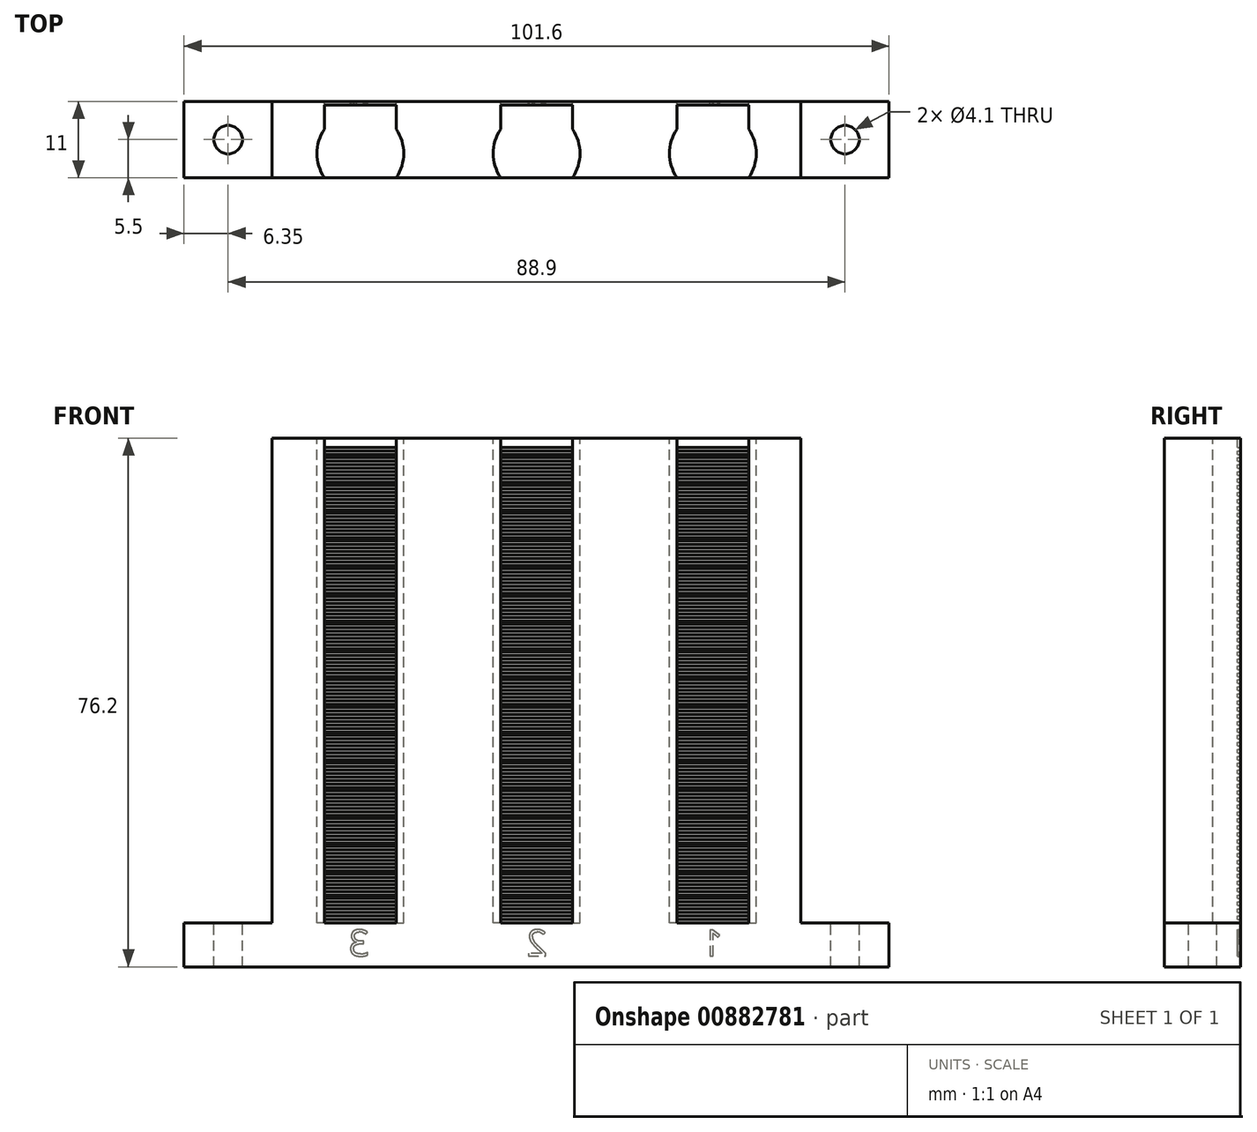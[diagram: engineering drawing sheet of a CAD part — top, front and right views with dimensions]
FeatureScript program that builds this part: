
annotation { "Feature Type Name" : "Feature", "Feature Type Description" : "" }
export const myFeature = defineFeature(function(context is Context, id is Id, definition is map)
    precondition{}
    {
        {
            var Q0;
            Q0=qCreatedBy(makeId("Top.planeOp"),FACE);
            var sketch = newSketch(context, id + "F0", { "sketchPlane" : qUnion([Q0])});
            skLineSegment(sketch, "E0.bottom", {"start": v(38.1, -5.5) * mm, "end": v(-38.1, -5.5) * mm});
            skLineSegment(sketch, "E0.top", {"start": v(38.1, 5.5) * mm, "end": v(-38.1, 5.5) * mm});
            skLineSegment(sketch, "E0.left", {"start": v(38.1, -5.5) * mm, "end": v(38.1, 5.5) * mm});
            skLineSegment(sketch, "E0.right", {"start": v(-38.1, -5.5) * mm, "end": v(-38.1, 5.5) * mm});
            skPoint(sketch, "E0.middle", {"position": v(0, 0) * mm});
            skSolve(sketch);
        }
        {
            var Q0;
            Q0 = qSketchRegion(id + "F0", true);
            extrude(context, id + "F1", {"entities" : qUnion([Q0]), "depth" : 76.2 * mm, "offsetDistance" : 25.4 * mm});
        }
        {
            var Q0;
            Q0=makeQuery(id+"F1.opExtrude","CAP_FACE",FACE,{"disambiguationData":[OSD([sQuery(id+"F0.wireOp",EDGE,"E0.bottom"),sQuery(id+"F0.wireOp",EDGE,"E0.top"),sQuery(id+"F0.wireOp",EDGE,"E0.left"),sQuery(id+"F0.wireOp",EDGE,"E0.right")])],"isStart":false});
            var sketch = newSketch(context, id + "F2", { "sketchPlane" : qUnion([Q0])});
            skLineSegment(sketch, "E1", {"start": v(0, 5.5) * mm, "end": v(0, -5.5) * mm});
            skCircle(sketch, "E2", {"center": v(0, -2) * mm, "radius": 6.25 * mm});
            skCircle(sketch, "E3", {"center": v(-25.4, -2) * mm, "radius": 6.25 * mm});
            skCircle(sketch, "E4", {"center": v(25.4, -2) * mm, "radius": 6.25 * mm});
            skSolve(sketch);
        }
        {
            var Q0;
            Q0 = qSketchRegion(id + "F2", true);
            extrude(context, id + "F3", {"entities" : qUnion([Q0]), "operationType" : NewBodyOperationType.REMOVE, "oppositeDirection" : true, "depth" : 69.85 * mm, "offsetDistance" : 25.4 * mm});
        }
        {
            var Q0;
            Q0=makeQuery(id+"F1.opExtrude","SWEPT_FACE",FACE,{"disambiguationData":[OSD([sQuery(id+"F0.wireOp",EDGE,"E0.top")])]});
            var sketch = newSketch(context, id + "F4", { "sketchPlane" : qUnion([Q0])});
            skLineSegment(sketch, "E5.bottom", {"start": v(-30.58, 6.35) * mm, "end": v(-20.22, 6.35) * mm});
            skLineSegment(sketch, "E5.top", {"start": v(-30.58, 6.85) * mm, "end": v(-20.22, 6.85) * mm});
            skLineSegment(sketch, "E5.left", {"start": v(-30.58, 6.35) * mm, "end": v(-30.58, 6.85) * mm});
            skLineSegment(sketch, "E5.right", {"start": v(-20.22, 6.35) * mm, "end": v(-20.22, 6.85) * mm});
            skLineSegment(sketch, "E6.0.1.0", {"start": v(-30.58, 7.35) * mm, "end": v(-20.22, 7.35) * mm});
            skLineSegment(sketch, "E6.0.1.1", {"start": v(-30.58, 7.85) * mm, "end": v(-20.22, 7.85) * mm});
            skLineSegment(sketch, "E6.0.1.2", {"start": v(-30.58, 7.35) * mm, "end": v(-30.58, 7.85) * mm});
            skLineSegment(sketch, "E6.0.1.3", {"start": v(-20.22, 7.35) * mm, "end": v(-20.22, 7.85) * mm});
            skLineSegment(sketch, "E6.0.2.0", {"start": v(-30.58, 8.35) * mm, "end": v(-20.22, 8.35) * mm});
            skLineSegment(sketch, "E6.0.2.1", {"start": v(-30.58, 8.85) * mm, "end": v(-20.22, 8.85) * mm});
            skLineSegment(sketch, "E6.0.2.2", {"start": v(-30.58, 8.35) * mm, "end": v(-30.58, 8.85) * mm});
            skLineSegment(sketch, "E6.0.2.3", {"start": v(-20.22, 8.35) * mm, "end": v(-20.22, 8.85) * mm});
            skLineSegment(sketch, "E6.0.3.0", {"start": v(-30.58, 9.35) * mm, "end": v(-20.22, 9.35) * mm});
            skLineSegment(sketch, "E6.0.3.1", {"start": v(-30.58, 9.85) * mm, "end": v(-20.22, 9.85) * mm});
            skLineSegment(sketch, "E6.0.3.2", {"start": v(-30.58, 9.35) * mm, "end": v(-30.58, 9.85) * mm});
            skLineSegment(sketch, "E6.0.3.3", {"start": v(-20.22, 9.35) * mm, "end": v(-20.22, 9.85) * mm});
            skLineSegment(sketch, "E6.0.4.0", {"start": v(-30.58, 10.35) * mm, "end": v(-20.22, 10.35) * mm});
            skLineSegment(sketch, "E6.0.4.1", {"start": v(-30.58, 10.85) * mm, "end": v(-20.22, 10.85) * mm});
            skLineSegment(sketch, "E6.0.4.2", {"start": v(-30.58, 10.35) * mm, "end": v(-30.58, 10.85) * mm});
            skLineSegment(sketch, "E6.0.4.3", {"start": v(-20.22, 10.35) * mm, "end": v(-20.22, 10.85) * mm});
            skLineSegment(sketch, "E6.0.5.0", {"start": v(-30.58, 11.35) * mm, "end": v(-20.22, 11.35) * mm});
            skLineSegment(sketch, "E6.0.5.1", {"start": v(-30.58, 11.85) * mm, "end": v(-20.22, 11.85) * mm});
            skLineSegment(sketch, "E6.0.5.2", {"start": v(-30.58, 11.35) * mm, "end": v(-30.58, 11.85) * mm});
            skLineSegment(sketch, "E6.0.5.3", {"start": v(-20.22, 11.35) * mm, "end": v(-20.22, 11.85) * mm});
            skLineSegment(sketch, "E6.0.6.0", {"start": v(-30.58, 12.35) * mm, "end": v(-20.22, 12.35) * mm});
            skLineSegment(sketch, "E6.0.6.1", {"start": v(-30.58, 12.85) * mm, "end": v(-20.22, 12.85) * mm});
            skLineSegment(sketch, "E6.0.6.2", {"start": v(-30.58, 12.35) * mm, "end": v(-30.58, 12.85) * mm});
            skLineSegment(sketch, "E6.0.6.3", {"start": v(-20.22, 12.35) * mm, "end": v(-20.22, 12.85) * mm});
            skLineSegment(sketch, "E6.0.7.0", {"start": v(-30.58, 13.35) * mm, "end": v(-20.22, 13.35) * mm});
            skLineSegment(sketch, "E6.0.7.1", {"start": v(-30.58, 13.85) * mm, "end": v(-20.22, 13.85) * mm});
            skLineSegment(sketch, "E6.0.7.2", {"start": v(-30.58, 13.35) * mm, "end": v(-30.58, 13.85) * mm});
            skLineSegment(sketch, "E6.0.7.3", {"start": v(-20.22, 13.35) * mm, "end": v(-20.22, 13.85) * mm});
            skLineSegment(sketch, "E6.0.8.0", {"start": v(-30.58, 14.35) * mm, "end": v(-20.22, 14.35) * mm});
            skLineSegment(sketch, "E6.0.8.1", {"start": v(-30.58, 14.85) * mm, "end": v(-20.22, 14.85) * mm});
            skLineSegment(sketch, "E6.0.8.2", {"start": v(-30.58, 14.35) * mm, "end": v(-30.58, 14.85) * mm});
            skLineSegment(sketch, "E6.0.8.3", {"start": v(-20.22, 14.35) * mm, "end": v(-20.22, 14.85) * mm});
            skLineSegment(sketch, "E6.0.9.0", {"start": v(-30.58, 15.35) * mm, "end": v(-20.22, 15.35) * mm});
            skLineSegment(sketch, "E6.0.9.1", {"start": v(-30.58, 15.85) * mm, "end": v(-20.22, 15.85) * mm});
            skLineSegment(sketch, "E6.0.9.2", {"start": v(-30.58, 15.35) * mm, "end": v(-30.58, 15.85) * mm});
            skLineSegment(sketch, "E6.0.9.3", {"start": v(-20.22, 15.35) * mm, "end": v(-20.22, 15.85) * mm});
            skLineSegment(sketch, "E6.0.10.0", {"start": v(-30.58, 16.35) * mm, "end": v(-20.22, 16.35) * mm});
            skLineSegment(sketch, "E6.0.10.1", {"start": v(-30.58, 16.85) * mm, "end": v(-20.22, 16.85) * mm});
            skLineSegment(sketch, "E6.0.10.2", {"start": v(-30.58, 16.35) * mm, "end": v(-30.58, 16.85) * mm});
            skLineSegment(sketch, "E6.0.10.3", {"start": v(-20.22, 16.35) * mm, "end": v(-20.22, 16.85) * mm});
            skLineSegment(sketch, "E6.0.11.0", {"start": v(-30.58, 17.35) * mm, "end": v(-20.22, 17.35) * mm});
            skLineSegment(sketch, "E6.0.11.1", {"start": v(-30.58, 17.85) * mm, "end": v(-20.22, 17.85) * mm});
            skLineSegment(sketch, "E6.0.11.2", {"start": v(-30.58, 17.35) * mm, "end": v(-30.58, 17.85) * mm});
            skLineSegment(sketch, "E6.0.11.3", {"start": v(-20.22, 17.35) * mm, "end": v(-20.22, 17.85) * mm});
            skLineSegment(sketch, "E6.0.12.0", {"start": v(-30.58, 18.35) * mm, "end": v(-20.22, 18.35) * mm});
            skLineSegment(sketch, "E6.0.12.1", {"start": v(-30.58, 18.85) * mm, "end": v(-20.22, 18.85) * mm});
            skLineSegment(sketch, "E6.0.12.2", {"start": v(-30.58, 18.35) * mm, "end": v(-30.58, 18.85) * mm});
            skLineSegment(sketch, "E6.0.12.3", {"start": v(-20.22, 18.35) * mm, "end": v(-20.22, 18.85) * mm});
            skLineSegment(sketch, "E6.0.13.0", {"start": v(-30.58, 19.35) * mm, "end": v(-20.22, 19.35) * mm});
            skLineSegment(sketch, "E6.0.13.1", {"start": v(-30.58, 19.85) * mm, "end": v(-20.22, 19.85) * mm});
            skLineSegment(sketch, "E6.0.13.2", {"start": v(-30.58, 19.35) * mm, "end": v(-30.58, 19.85) * mm});
            skLineSegment(sketch, "E6.0.13.3", {"start": v(-20.22, 19.35) * mm, "end": v(-20.22, 19.85) * mm});
            skLineSegment(sketch, "E6.0.14.0", {"start": v(-30.58, 20.35) * mm, "end": v(-20.22, 20.35) * mm});
            skLineSegment(sketch, "E6.0.14.1", {"start": v(-30.58, 20.85) * mm, "end": v(-20.22, 20.85) * mm});
            skLineSegment(sketch, "E6.0.14.2", {"start": v(-30.58, 20.35) * mm, "end": v(-30.58, 20.85) * mm});
            skLineSegment(sketch, "E6.0.14.3", {"start": v(-20.22, 20.35) * mm, "end": v(-20.22, 20.85) * mm});
            skLineSegment(sketch, "E6.0.15.0", {"start": v(-30.58, 21.35) * mm, "end": v(-20.22, 21.35) * mm});
            skLineSegment(sketch, "E6.0.15.1", {"start": v(-30.58, 21.85) * mm, "end": v(-20.22, 21.85) * mm});
            skLineSegment(sketch, "E6.0.15.2", {"start": v(-30.58, 21.35) * mm, "end": v(-30.58, 21.85) * mm});
            skLineSegment(sketch, "E6.0.15.3", {"start": v(-20.22, 21.35) * mm, "end": v(-20.22, 21.85) * mm});
            skLineSegment(sketch, "E6.1.0.0", {"start": v(-5.18, 6.35) * mm, "end": v(5.18, 6.35) * mm});
            skLineSegment(sketch, "E6.1.0.1", {"start": v(-5.18, 6.85) * mm, "end": v(5.18, 6.85) * mm});
            skLineSegment(sketch, "E6.1.0.2", {"start": v(-5.18, 6.35) * mm, "end": v(-5.18, 6.85) * mm});
            skLineSegment(sketch, "E6.1.0.3", {"start": v(5.18, 6.35) * mm, "end": v(5.18, 6.85) * mm});
            skLineSegment(sketch, "E6.1.1.0", {"start": v(-5.18, 7.35) * mm, "end": v(5.18, 7.35) * mm});
            skLineSegment(sketch, "E6.1.1.1", {"start": v(-5.18, 7.85) * mm, "end": v(5.18, 7.85) * mm});
            skLineSegment(sketch, "E6.1.1.2", {"start": v(-5.18, 7.35) * mm, "end": v(-5.18, 7.85) * mm});
            skLineSegment(sketch, "E6.1.1.3", {"start": v(5.18, 7.35) * mm, "end": v(5.18, 7.85) * mm});
            skLineSegment(sketch, "E6.1.2.0", {"start": v(-5.18, 8.35) * mm, "end": v(5.18, 8.35) * mm});
            skLineSegment(sketch, "E6.1.2.1", {"start": v(-5.18, 8.85) * mm, "end": v(5.18, 8.85) * mm});
            skLineSegment(sketch, "E6.1.2.2", {"start": v(-5.18, 8.35) * mm, "end": v(-5.18, 8.85) * mm});
            skLineSegment(sketch, "E6.1.2.3", {"start": v(5.18, 8.35) * mm, "end": v(5.18, 8.85) * mm});
            skLineSegment(sketch, "E6.1.3.0", {"start": v(-5.18, 9.35) * mm, "end": v(5.18, 9.35) * mm});
            skLineSegment(sketch, "E6.1.3.1", {"start": v(-5.18, 9.85) * mm, "end": v(5.18, 9.85) * mm});
            skLineSegment(sketch, "E6.1.3.2", {"start": v(-5.18, 9.35) * mm, "end": v(-5.18, 9.85) * mm});
            skLineSegment(sketch, "E6.1.3.3", {"start": v(5.18, 9.35) * mm, "end": v(5.18, 9.85) * mm});
            skLineSegment(sketch, "E6.1.4.0", {"start": v(-5.18, 10.35) * mm, "end": v(5.18, 10.35) * mm});
            skLineSegment(sketch, "E6.1.4.1", {"start": v(-5.18, 10.85) * mm, "end": v(5.18, 10.85) * mm});
            skLineSegment(sketch, "E6.1.4.2", {"start": v(-5.18, 10.35) * mm, "end": v(-5.18, 10.85) * mm});
            skLineSegment(sketch, "E6.1.4.3", {"start": v(5.18, 10.35) * mm, "end": v(5.18, 10.85) * mm});
            skLineSegment(sketch, "E6.1.5.0", {"start": v(-5.18, 11.35) * mm, "end": v(5.18, 11.35) * mm});
            skLineSegment(sketch, "E6.1.5.1", {"start": v(-5.18, 11.85) * mm, "end": v(5.18, 11.85) * mm});
            skLineSegment(sketch, "E6.1.5.2", {"start": v(-5.18, 11.35) * mm, "end": v(-5.18, 11.85) * mm});
            skLineSegment(sketch, "E6.1.5.3", {"start": v(5.18, 11.35) * mm, "end": v(5.18, 11.85) * mm});
            skLineSegment(sketch, "E6.1.6.0", {"start": v(-5.18, 12.35) * mm, "end": v(5.18, 12.35) * mm});
            skLineSegment(sketch, "E6.1.6.1", {"start": v(-5.18, 12.85) * mm, "end": v(5.18, 12.85) * mm});
            skLineSegment(sketch, "E6.1.6.2", {"start": v(-5.18, 12.35) * mm, "end": v(-5.18, 12.85) * mm});
            skLineSegment(sketch, "E6.1.6.3", {"start": v(5.18, 12.35) * mm, "end": v(5.18, 12.85) * mm});
            skLineSegment(sketch, "E6.1.7.0", {"start": v(-5.18, 13.35) * mm, "end": v(5.18, 13.35) * mm});
            skLineSegment(sketch, "E6.1.7.1", {"start": v(-5.18, 13.85) * mm, "end": v(5.18, 13.85) * mm});
            skLineSegment(sketch, "E6.1.7.2", {"start": v(-5.18, 13.35) * mm, "end": v(-5.18, 13.85) * mm});
            skLineSegment(sketch, "E6.1.7.3", {"start": v(5.18, 13.35) * mm, "end": v(5.18, 13.85) * mm});
            skLineSegment(sketch, "E6.1.8.0", {"start": v(-5.18, 14.35) * mm, "end": v(5.18, 14.35) * mm});
            skLineSegment(sketch, "E6.1.8.1", {"start": v(-5.18, 14.85) * mm, "end": v(5.18, 14.85) * mm});
            skLineSegment(sketch, "E6.1.8.2", {"start": v(-5.18, 14.35) * mm, "end": v(-5.18, 14.85) * mm});
            skLineSegment(sketch, "E6.1.8.3", {"start": v(5.18, 14.35) * mm, "end": v(5.18, 14.85) * mm});
            skLineSegment(sketch, "E6.1.9.0", {"start": v(-5.18, 15.35) * mm, "end": v(5.18, 15.35) * mm});
            skLineSegment(sketch, "E6.1.9.1", {"start": v(-5.18, 15.85) * mm, "end": v(5.18, 15.85) * mm});
            skLineSegment(sketch, "E6.1.9.2", {"start": v(-5.18, 15.35) * mm, "end": v(-5.18, 15.85) * mm});
            skLineSegment(sketch, "E6.1.9.3", {"start": v(5.18, 15.35) * mm, "end": v(5.18, 15.85) * mm});
            skLineSegment(sketch, "E6.1.10.0", {"start": v(-5.18, 16.35) * mm, "end": v(5.18, 16.35) * mm});
            skLineSegment(sketch, "E6.1.10.1", {"start": v(-5.18, 16.85) * mm, "end": v(5.18, 16.85) * mm});
            skLineSegment(sketch, "E6.1.10.2", {"start": v(-5.18, 16.35) * mm, "end": v(-5.18, 16.85) * mm});
            skLineSegment(sketch, "E6.1.10.3", {"start": v(5.18, 16.35) * mm, "end": v(5.18, 16.85) * mm});
            skLineSegment(sketch, "E6.1.11.0", {"start": v(-5.18, 17.35) * mm, "end": v(5.18, 17.35) * mm});
            skLineSegment(sketch, "E6.1.11.1", {"start": v(-5.18, 17.85) * mm, "end": v(5.18, 17.85) * mm});
            skLineSegment(sketch, "E6.1.11.2", {"start": v(-5.18, 17.35) * mm, "end": v(-5.18, 17.85) * mm});
            skLineSegment(sketch, "E6.1.11.3", {"start": v(5.18, 17.35) * mm, "end": v(5.18, 17.85) * mm});
            skLineSegment(sketch, "E6.1.12.0", {"start": v(-5.18, 18.35) * mm, "end": v(5.18, 18.35) * mm});
            skLineSegment(sketch, "E6.1.12.1", {"start": v(-5.18, 18.85) * mm, "end": v(5.18, 18.85) * mm});
            skLineSegment(sketch, "E6.1.12.2", {"start": v(-5.18, 18.35) * mm, "end": v(-5.18, 18.85) * mm});
            skLineSegment(sketch, "E6.1.12.3", {"start": v(5.18, 18.35) * mm, "end": v(5.18, 18.85) * mm});
            skLineSegment(sketch, "E6.1.13.0", {"start": v(-5.18, 19.35) * mm, "end": v(5.18, 19.35) * mm});
            skLineSegment(sketch, "E6.1.13.1", {"start": v(-5.18, 19.85) * mm, "end": v(5.18, 19.85) * mm});
            skLineSegment(sketch, "E6.1.13.2", {"start": v(-5.18, 19.35) * mm, "end": v(-5.18, 19.85) * mm});
            skLineSegment(sketch, "E6.1.13.3", {"start": v(5.18, 19.35) * mm, "end": v(5.18, 19.85) * mm});
            skLineSegment(sketch, "E6.1.14.0", {"start": v(-5.18, 20.35) * mm, "end": v(5.18, 20.35) * mm});
            skLineSegment(sketch, "E6.1.14.1", {"start": v(-5.18, 20.85) * mm, "end": v(5.18, 20.85) * mm});
            skLineSegment(sketch, "E6.1.14.2", {"start": v(-5.18, 20.35) * mm, "end": v(-5.18, 20.85) * mm});
            skLineSegment(sketch, "E6.1.14.3", {"start": v(5.18, 20.35) * mm, "end": v(5.18, 20.85) * mm});
            skLineSegment(sketch, "E6.1.15.0", {"start": v(-5.18, 21.35) * mm, "end": v(5.18, 21.35) * mm});
            skLineSegment(sketch, "E6.1.15.1", {"start": v(-5.18, 21.85) * mm, "end": v(5.18, 21.85) * mm});
            skLineSegment(sketch, "E6.1.15.2", {"start": v(-5.18, 21.35) * mm, "end": v(-5.18, 21.85) * mm});
            skLineSegment(sketch, "E6.1.15.3", {"start": v(5.18, 21.35) * mm, "end": v(5.18, 21.85) * mm});
            skLineSegment(sketch, "E6.2.0.0", {"start": v(20.22, 6.35) * mm, "end": v(30.58, 6.35) * mm});
            skLineSegment(sketch, "E6.2.0.1", {"start": v(20.22, 6.85) * mm, "end": v(30.58, 6.85) * mm});
            skLineSegment(sketch, "E6.2.0.2", {"start": v(20.22, 6.35) * mm, "end": v(20.22, 6.85) * mm});
            skLineSegment(sketch, "E6.2.0.3", {"start": v(30.58, 6.35) * mm, "end": v(30.58, 6.85) * mm});
            skLineSegment(sketch, "E6.2.1.0", {"start": v(20.22, 7.35) * mm, "end": v(30.58, 7.35) * mm});
            skLineSegment(sketch, "E6.2.1.1", {"start": v(20.22, 7.85) * mm, "end": v(30.58, 7.85) * mm});
            skLineSegment(sketch, "E6.2.1.2", {"start": v(20.22, 7.35) * mm, "end": v(20.22, 7.85) * mm});
            skLineSegment(sketch, "E6.2.1.3", {"start": v(30.58, 7.35) * mm, "end": v(30.58, 7.85) * mm});
            skLineSegment(sketch, "E6.2.2.0", {"start": v(20.22, 8.35) * mm, "end": v(30.58, 8.35) * mm});
            skLineSegment(sketch, "E6.2.2.1", {"start": v(20.22, 8.85) * mm, "end": v(30.58, 8.85) * mm});
            skLineSegment(sketch, "E6.2.2.2", {"start": v(20.22, 8.35) * mm, "end": v(20.22, 8.85) * mm});
            skLineSegment(sketch, "E6.2.2.3", {"start": v(30.58, 8.35) * mm, "end": v(30.58, 8.85) * mm});
            skLineSegment(sketch, "E6.2.3.0", {"start": v(20.22, 9.35) * mm, "end": v(30.58, 9.35) * mm});
            skLineSegment(sketch, "E6.2.3.1", {"start": v(20.22, 9.85) * mm, "end": v(30.58, 9.85) * mm});
            skLineSegment(sketch, "E6.2.3.2", {"start": v(20.22, 9.35) * mm, "end": v(20.22, 9.85) * mm});
            skLineSegment(sketch, "E6.2.3.3", {"start": v(30.58, 9.35) * mm, "end": v(30.58, 9.85) * mm});
            skLineSegment(sketch, "E6.2.4.0", {"start": v(20.22, 10.35) * mm, "end": v(30.58, 10.35) * mm});
            skLineSegment(sketch, "E6.2.4.1", {"start": v(20.22, 10.85) * mm, "end": v(30.58, 10.85) * mm});
            skLineSegment(sketch, "E6.2.4.2", {"start": v(20.22, 10.35) * mm, "end": v(20.22, 10.85) * mm});
            skLineSegment(sketch, "E6.2.4.3", {"start": v(30.58, 10.35) * mm, "end": v(30.58, 10.85) * mm});
            skLineSegment(sketch, "E6.2.5.0", {"start": v(20.22, 11.35) * mm, "end": v(30.58, 11.35) * mm});
            skLineSegment(sketch, "E6.2.5.1", {"start": v(20.22, 11.85) * mm, "end": v(30.58, 11.85) * mm});
            skLineSegment(sketch, "E6.2.5.2", {"start": v(20.22, 11.35) * mm, "end": v(20.22, 11.85) * mm});
            skLineSegment(sketch, "E6.2.5.3", {"start": v(30.58, 11.35) * mm, "end": v(30.58, 11.85) * mm});
            skLineSegment(sketch, "E6.2.6.0", {"start": v(20.22, 12.35) * mm, "end": v(30.58, 12.35) * mm});
            skLineSegment(sketch, "E6.2.6.1", {"start": v(20.22, 12.85) * mm, "end": v(30.58, 12.85) * mm});
            skLineSegment(sketch, "E6.2.6.2", {"start": v(20.22, 12.35) * mm, "end": v(20.22, 12.85) * mm});
            skLineSegment(sketch, "E6.2.6.3", {"start": v(30.58, 12.35) * mm, "end": v(30.58, 12.85) * mm});
            skLineSegment(sketch, "E6.2.7.0", {"start": v(20.22, 13.35) * mm, "end": v(30.58, 13.35) * mm});
            skLineSegment(sketch, "E6.2.7.1", {"start": v(20.22, 13.85) * mm, "end": v(30.58, 13.85) * mm});
            skLineSegment(sketch, "E6.2.7.2", {"start": v(20.22, 13.35) * mm, "end": v(20.22, 13.85) * mm});
            skLineSegment(sketch, "E6.2.7.3", {"start": v(30.58, 13.35) * mm, "end": v(30.58, 13.85) * mm});
            skLineSegment(sketch, "E6.2.8.0", {"start": v(20.22, 14.35) * mm, "end": v(30.58, 14.35) * mm});
            skLineSegment(sketch, "E6.2.8.1", {"start": v(20.22, 14.85) * mm, "end": v(30.58, 14.85) * mm});
            skLineSegment(sketch, "E6.2.8.2", {"start": v(20.22, 14.35) * mm, "end": v(20.22, 14.85) * mm});
            skLineSegment(sketch, "E6.2.8.3", {"start": v(30.58, 14.35) * mm, "end": v(30.58, 14.85) * mm});
            skLineSegment(sketch, "E6.2.9.0", {"start": v(20.22, 15.35) * mm, "end": v(30.58, 15.35) * mm});
            skLineSegment(sketch, "E6.2.9.1", {"start": v(20.22, 15.85) * mm, "end": v(30.58, 15.85) * mm});
            skLineSegment(sketch, "E6.2.9.2", {"start": v(20.22, 15.35) * mm, "end": v(20.22, 15.85) * mm});
            skLineSegment(sketch, "E6.2.9.3", {"start": v(30.58, 15.35) * mm, "end": v(30.58, 15.85) * mm});
            skLineSegment(sketch, "E6.2.10.0", {"start": v(20.22, 16.35) * mm, "end": v(30.58, 16.35) * mm});
            skLineSegment(sketch, "E6.2.10.1", {"start": v(20.22, 16.85) * mm, "end": v(30.58, 16.85) * mm});
            skLineSegment(sketch, "E6.2.10.2", {"start": v(20.22, 16.35) * mm, "end": v(20.22, 16.85) * mm});
            skLineSegment(sketch, "E6.2.10.3", {"start": v(30.58, 16.35) * mm, "end": v(30.58, 16.85) * mm});
            skLineSegment(sketch, "E6.2.11.0", {"start": v(20.22, 17.35) * mm, "end": v(30.58, 17.35) * mm});
            skLineSegment(sketch, "E6.2.11.1", {"start": v(20.22, 17.85) * mm, "end": v(30.58, 17.85) * mm});
            skLineSegment(sketch, "E6.2.11.2", {"start": v(20.22, 17.35) * mm, "end": v(20.22, 17.85) * mm});
            skLineSegment(sketch, "E6.2.11.3", {"start": v(30.58, 17.35) * mm, "end": v(30.58, 17.85) * mm});
            skLineSegment(sketch, "E6.2.12.0", {"start": v(20.22, 18.35) * mm, "end": v(30.58, 18.35) * mm});
            skLineSegment(sketch, "E6.2.12.1", {"start": v(20.22, 18.85) * mm, "end": v(30.58, 18.85) * mm});
            skLineSegment(sketch, "E6.2.12.2", {"start": v(20.22, 18.35) * mm, "end": v(20.22, 18.85) * mm});
            skLineSegment(sketch, "E6.2.12.3", {"start": v(30.58, 18.35) * mm, "end": v(30.58, 18.85) * mm});
            skLineSegment(sketch, "E6.2.13.0", {"start": v(20.22, 19.35) * mm, "end": v(30.58, 19.35) * mm});
            skLineSegment(sketch, "E6.2.13.1", {"start": v(20.22, 19.85) * mm, "end": v(30.58, 19.85) * mm});
            skLineSegment(sketch, "E6.2.13.2", {"start": v(20.22, 19.35) * mm, "end": v(20.22, 19.85) * mm});
            skLineSegment(sketch, "E6.2.13.3", {"start": v(30.58, 19.35) * mm, "end": v(30.58, 19.85) * mm});
            skLineSegment(sketch, "E6.2.14.0", {"start": v(20.22, 20.35) * mm, "end": v(30.58, 20.35) * mm});
            skLineSegment(sketch, "E6.2.14.1", {"start": v(20.22, 20.85) * mm, "end": v(30.58, 20.85) * mm});
            skLineSegment(sketch, "E6.2.14.2", {"start": v(20.22, 20.35) * mm, "end": v(20.22, 20.85) * mm});
            skLineSegment(sketch, "E6.2.14.3", {"start": v(30.58, 20.35) * mm, "end": v(30.58, 20.85) * mm});
            skLineSegment(sketch, "E6.2.15.0", {"start": v(20.22, 21.35) * mm, "end": v(30.58, 21.35) * mm});
            skLineSegment(sketch, "E6.2.15.1", {"start": v(20.22, 21.85) * mm, "end": v(30.58, 21.85) * mm});
            skLineSegment(sketch, "E6.2.15.2", {"start": v(20.22, 21.35) * mm, "end": v(20.22, 21.85) * mm});
            skLineSegment(sketch, "E6.2.15.3", {"start": v(30.58, 21.35) * mm, "end": v(30.58, 21.85) * mm});
            skLineSegment(sketch, "E6.direction1", {"start": v(-30.58, 6.35) * mm, "end": v(-5.18, 6.35) * mm, "construction": true});
            skLineSegment(sketch, "E6.direction2", {"start": v(-30.58, 6.35) * mm, "end": v(-30.58, 7.35) * mm, "construction": true});
            skLineSegment(sketch, "E7.0.0.16", {"start": v(-30.58, 22.35) * mm, "end": v(-20.22, 22.35) * mm});
            skLineSegment(sketch, "E7.3.0.16", {"start": v(-30.58, 22.85) * mm, "end": v(-20.22, 22.85) * mm});
            skLineSegment(sketch, "E7.6.0.16", {"start": v(-30.58, 22.35) * mm, "end": v(-30.58, 22.85) * mm});
            skLineSegment(sketch, "E7.9.0.16", {"start": v(-20.22, 22.35) * mm, "end": v(-20.22, 22.85) * mm});
            skLineSegment(sketch, "E7.0.0.17", {"start": v(-30.58, 23.35) * mm, "end": v(-20.22, 23.35) * mm});
            skLineSegment(sketch, "E7.3.0.17", {"start": v(-30.58, 23.85) * mm, "end": v(-20.22, 23.85) * mm});
            skLineSegment(sketch, "E7.6.0.17", {"start": v(-30.58, 23.35) * mm, "end": v(-30.58, 23.85) * mm});
            skLineSegment(sketch, "E7.9.0.17", {"start": v(-20.22, 23.35) * mm, "end": v(-20.22, 23.85) * mm});
            skLineSegment(sketch, "E7.0.1.16", {"start": v(-5.18, 22.35) * mm, "end": v(5.18, 22.35) * mm});
            skLineSegment(sketch, "E7.3.1.16", {"start": v(-5.18, 22.85) * mm, "end": v(5.18, 22.85) * mm});
            skLineSegment(sketch, "E7.6.1.16", {"start": v(-5.18, 22.35) * mm, "end": v(-5.18, 22.85) * mm});
            skLineSegment(sketch, "E7.9.1.16", {"start": v(5.18, 22.35) * mm, "end": v(5.18, 22.85) * mm});
            skLineSegment(sketch, "E7.0.1.17", {"start": v(-5.18, 23.35) * mm, "end": v(5.18, 23.35) * mm});
            skLineSegment(sketch, "E7.3.1.17", {"start": v(-5.18, 23.85) * mm, "end": v(5.18, 23.85) * mm});
            skLineSegment(sketch, "E7.6.1.17", {"start": v(-5.18, 23.35) * mm, "end": v(-5.18, 23.85) * mm});
            skLineSegment(sketch, "E7.9.1.17", {"start": v(5.18, 23.35) * mm, "end": v(5.18, 23.85) * mm});
            skLineSegment(sketch, "E7.0.2.16", {"start": v(20.22, 22.35) * mm, "end": v(30.58, 22.35) * mm});
            skLineSegment(sketch, "E7.3.2.16", {"start": v(20.22, 22.85) * mm, "end": v(30.58, 22.85) * mm});
            skLineSegment(sketch, "E7.6.2.16", {"start": v(20.22, 22.35) * mm, "end": v(20.22, 22.85) * mm});
            skLineSegment(sketch, "E7.9.2.16", {"start": v(30.58, 22.35) * mm, "end": v(30.58, 22.85) * mm});
            skLineSegment(sketch, "E7.0.2.17", {"start": v(20.22, 23.35) * mm, "end": v(30.58, 23.35) * mm});
            skLineSegment(sketch, "E7.3.2.17", {"start": v(20.22, 23.85) * mm, "end": v(30.58, 23.85) * mm});
            skLineSegment(sketch, "E7.6.2.17", {"start": v(20.22, 23.35) * mm, "end": v(20.22, 23.85) * mm});
            skLineSegment(sketch, "E7.9.2.17", {"start": v(30.58, 23.35) * mm, "end": v(30.58, 23.85) * mm});
            skLineSegment(sketch, "E8.0.0.18", {"start": v(-30.58, 24.35) * mm, "end": v(-20.22, 24.35) * mm});
            skLineSegment(sketch, "E8.3.0.18", {"start": v(-30.58, 24.85) * mm, "end": v(-20.22, 24.85) * mm});
            skLineSegment(sketch, "E8.6.0.18", {"start": v(-30.58, 24.35) * mm, "end": v(-30.58, 24.85) * mm});
            skLineSegment(sketch, "E8.9.0.18", {"start": v(-20.22, 24.35) * mm, "end": v(-20.22, 24.85) * mm});
            skLineSegment(sketch, "E8.0.0.19", {"start": v(-30.58, 25.35) * mm, "end": v(-20.22, 25.35) * mm});
            skLineSegment(sketch, "E8.3.0.19", {"start": v(-30.58, 25.85) * mm, "end": v(-20.22, 25.85) * mm});
            skLineSegment(sketch, "E8.6.0.19", {"start": v(-30.58, 25.35) * mm, "end": v(-30.58, 25.85) * mm});
            skLineSegment(sketch, "E8.9.0.19", {"start": v(-20.22, 25.35) * mm, "end": v(-20.22, 25.85) * mm});
            skLineSegment(sketch, "E8.0.0.20", {"start": v(-30.58, 26.35) * mm, "end": v(-20.22, 26.35) * mm});
            skLineSegment(sketch, "E8.3.0.20", {"start": v(-30.58, 26.85) * mm, "end": v(-20.22, 26.85) * mm});
            skLineSegment(sketch, "E8.6.0.20", {"start": v(-30.58, 26.35) * mm, "end": v(-30.58, 26.85) * mm});
            skLineSegment(sketch, "E8.9.0.20", {"start": v(-20.22, 26.35) * mm, "end": v(-20.22, 26.85) * mm});
            skLineSegment(sketch, "E8.0.0.21", {"start": v(-30.58, 27.35) * mm, "end": v(-20.22, 27.35) * mm});
            skLineSegment(sketch, "E8.3.0.21", {"start": v(-30.58, 27.85) * mm, "end": v(-20.22, 27.85) * mm});
            skLineSegment(sketch, "E8.6.0.21", {"start": v(-30.58, 27.35) * mm, "end": v(-30.58, 27.85) * mm});
            skLineSegment(sketch, "E8.9.0.21", {"start": v(-20.22, 27.35) * mm, "end": v(-20.22, 27.85) * mm});
            skLineSegment(sketch, "E8.0.0.22", {"start": v(-30.58, 28.35) * mm, "end": v(-20.22, 28.35) * mm});
            skLineSegment(sketch, "E8.3.0.22", {"start": v(-30.58, 28.85) * mm, "end": v(-20.22, 28.85) * mm});
            skLineSegment(sketch, "E8.6.0.22", {"start": v(-30.58, 28.35) * mm, "end": v(-30.58, 28.85) * mm});
            skLineSegment(sketch, "E8.9.0.22", {"start": v(-20.22, 28.35) * mm, "end": v(-20.22, 28.85) * mm});
            skLineSegment(sketch, "E8.0.0.23", {"start": v(-30.58, 29.35) * mm, "end": v(-20.22, 29.35) * mm});
            skLineSegment(sketch, "E8.3.0.23", {"start": v(-30.58, 29.85) * mm, "end": v(-20.22, 29.85) * mm});
            skLineSegment(sketch, "E8.6.0.23", {"start": v(-30.58, 29.35) * mm, "end": v(-30.58, 29.85) * mm});
            skLineSegment(sketch, "E8.9.0.23", {"start": v(-20.22, 29.35) * mm, "end": v(-20.22, 29.85) * mm});
            skLineSegment(sketch, "E8.0.0.24", {"start": v(-30.58, 30.35) * mm, "end": v(-20.22, 30.35) * mm});
            skLineSegment(sketch, "E8.3.0.24", {"start": v(-30.58, 30.85) * mm, "end": v(-20.22, 30.85) * mm});
            skLineSegment(sketch, "E8.6.0.24", {"start": v(-30.58, 30.35) * mm, "end": v(-30.58, 30.85) * mm});
            skLineSegment(sketch, "E8.9.0.24", {"start": v(-20.22, 30.35) * mm, "end": v(-20.22, 30.85) * mm});
            skLineSegment(sketch, "E8.0.0.25", {"start": v(-30.58, 31.35) * mm, "end": v(-20.22, 31.35) * mm});
            skLineSegment(sketch, "E8.3.0.25", {"start": v(-30.58, 31.85) * mm, "end": v(-20.22, 31.85) * mm});
            skLineSegment(sketch, "E8.6.0.25", {"start": v(-30.58, 31.35) * mm, "end": v(-30.58, 31.85) * mm});
            skLineSegment(sketch, "E8.9.0.25", {"start": v(-20.22, 31.35) * mm, "end": v(-20.22, 31.85) * mm});
            skLineSegment(sketch, "E8.0.0.26", {"start": v(-30.58, 32.35) * mm, "end": v(-20.22, 32.35) * mm});
            skLineSegment(sketch, "E8.3.0.26", {"start": v(-30.58, 32.85) * mm, "end": v(-20.22, 32.85) * mm});
            skLineSegment(sketch, "E8.6.0.26", {"start": v(-30.58, 32.35) * mm, "end": v(-30.58, 32.85) * mm});
            skLineSegment(sketch, "E8.9.0.26", {"start": v(-20.22, 32.35) * mm, "end": v(-20.22, 32.85) * mm});
            skLineSegment(sketch, "E8.0.0.27", {"start": v(-30.58, 33.35) * mm, "end": v(-20.22, 33.35) * mm});
            skLineSegment(sketch, "E8.3.0.27", {"start": v(-30.58, 33.85) * mm, "end": v(-20.22, 33.85) * mm});
            skLineSegment(sketch, "E8.6.0.27", {"start": v(-30.58, 33.35) * mm, "end": v(-30.58, 33.85) * mm});
            skLineSegment(sketch, "E8.9.0.27", {"start": v(-20.22, 33.35) * mm, "end": v(-20.22, 33.85) * mm});
            skLineSegment(sketch, "E8.0.0.28", {"start": v(-30.58, 34.35) * mm, "end": v(-20.22, 34.35) * mm});
            skLineSegment(sketch, "E8.3.0.28", {"start": v(-30.58, 34.85) * mm, "end": v(-20.22, 34.85) * mm});
            skLineSegment(sketch, "E8.6.0.28", {"start": v(-30.58, 34.35) * mm, "end": v(-30.58, 34.85) * mm});
            skLineSegment(sketch, "E8.9.0.28", {"start": v(-20.22, 34.35) * mm, "end": v(-20.22, 34.85) * mm});
            skLineSegment(sketch, "E8.0.0.29", {"start": v(-30.58, 35.35) * mm, "end": v(-20.22, 35.35) * mm});
            skLineSegment(sketch, "E8.3.0.29", {"start": v(-30.58, 35.85) * mm, "end": v(-20.22, 35.85) * mm});
            skLineSegment(sketch, "E8.6.0.29", {"start": v(-30.58, 35.35) * mm, "end": v(-30.58, 35.85) * mm});
            skLineSegment(sketch, "E8.9.0.29", {"start": v(-20.22, 35.35) * mm, "end": v(-20.22, 35.85) * mm});
            skLineSegment(sketch, "E8.0.0.30", {"start": v(-30.58, 36.35) * mm, "end": v(-20.22, 36.35) * mm});
            skLineSegment(sketch, "E8.3.0.30", {"start": v(-30.58, 36.85) * mm, "end": v(-20.22, 36.85) * mm});
            skLineSegment(sketch, "E8.6.0.30", {"start": v(-30.58, 36.35) * mm, "end": v(-30.58, 36.85) * mm});
            skLineSegment(sketch, "E8.9.0.30", {"start": v(-20.22, 36.35) * mm, "end": v(-20.22, 36.85) * mm});
            skLineSegment(sketch, "E8.0.0.31", {"start": v(-30.58, 37.35) * mm, "end": v(-20.22, 37.35) * mm});
            skLineSegment(sketch, "E8.3.0.31", {"start": v(-30.58, 37.85) * mm, "end": v(-20.22, 37.85) * mm});
            skLineSegment(sketch, "E8.6.0.31", {"start": v(-30.58, 37.35) * mm, "end": v(-30.58, 37.85) * mm});
            skLineSegment(sketch, "E8.9.0.31", {"start": v(-20.22, 37.35) * mm, "end": v(-20.22, 37.85) * mm});
            skLineSegment(sketch, "E8.0.0.32", {"start": v(-30.58, 38.35) * mm, "end": v(-20.22, 38.35) * mm});
            skLineSegment(sketch, "E8.3.0.32", {"start": v(-30.58, 38.85) * mm, "end": v(-20.22, 38.85) * mm});
            skLineSegment(sketch, "E8.6.0.32", {"start": v(-30.58, 38.35) * mm, "end": v(-30.58, 38.85) * mm});
            skLineSegment(sketch, "E8.9.0.32", {"start": v(-20.22, 38.35) * mm, "end": v(-20.22, 38.85) * mm});
            skLineSegment(sketch, "E8.0.0.33", {"start": v(-30.58, 39.35) * mm, "end": v(-20.22, 39.35) * mm});
            skLineSegment(sketch, "E8.3.0.33", {"start": v(-30.58, 39.85) * mm, "end": v(-20.22, 39.85) * mm});
            skLineSegment(sketch, "E8.6.0.33", {"start": v(-30.58, 39.35) * mm, "end": v(-30.58, 39.85) * mm});
            skLineSegment(sketch, "E8.9.0.33", {"start": v(-20.22, 39.35) * mm, "end": v(-20.22, 39.85) * mm});
            skLineSegment(sketch, "E8.0.0.34", {"start": v(-30.58, 40.35) * mm, "end": v(-20.22, 40.35) * mm});
            skLineSegment(sketch, "E8.3.0.34", {"start": v(-30.58, 40.85) * mm, "end": v(-20.22, 40.85) * mm});
            skLineSegment(sketch, "E8.6.0.34", {"start": v(-30.58, 40.35) * mm, "end": v(-30.58, 40.85) * mm});
            skLineSegment(sketch, "E8.9.0.34", {"start": v(-20.22, 40.35) * mm, "end": v(-20.22, 40.85) * mm});
            skLineSegment(sketch, "E8.0.0.35", {"start": v(-30.58, 41.35) * mm, "end": v(-20.22, 41.35) * mm});
            skLineSegment(sketch, "E8.3.0.35", {"start": v(-30.58, 41.85) * mm, "end": v(-20.22, 41.85) * mm});
            skLineSegment(sketch, "E8.6.0.35", {"start": v(-30.58, 41.35) * mm, "end": v(-30.58, 41.85) * mm});
            skLineSegment(sketch, "E8.9.0.35", {"start": v(-20.22, 41.35) * mm, "end": v(-20.22, 41.85) * mm});
            skLineSegment(sketch, "E8.0.0.36", {"start": v(-30.58, 42.35) * mm, "end": v(-20.22, 42.35) * mm});
            skLineSegment(sketch, "E8.3.0.36", {"start": v(-30.58, 42.85) * mm, "end": v(-20.22, 42.85) * mm});
            skLineSegment(sketch, "E8.6.0.36", {"start": v(-30.58, 42.35) * mm, "end": v(-30.58, 42.85) * mm});
            skLineSegment(sketch, "E8.9.0.36", {"start": v(-20.22, 42.35) * mm, "end": v(-20.22, 42.85) * mm});
            skLineSegment(sketch, "E8.0.0.37", {"start": v(-30.58, 43.35) * mm, "end": v(-20.22, 43.35) * mm});
            skLineSegment(sketch, "E8.3.0.37", {"start": v(-30.58, 43.85) * mm, "end": v(-20.22, 43.85) * mm});
            skLineSegment(sketch, "E8.6.0.37", {"start": v(-30.58, 43.35) * mm, "end": v(-30.58, 43.85) * mm});
            skLineSegment(sketch, "E8.9.0.37", {"start": v(-20.22, 43.35) * mm, "end": v(-20.22, 43.85) * mm});
            skLineSegment(sketch, "E8.0.0.38", {"start": v(-30.58, 44.35) * mm, "end": v(-20.22, 44.35) * mm});
            skLineSegment(sketch, "E8.3.0.38", {"start": v(-30.58, 44.85) * mm, "end": v(-20.22, 44.85) * mm});
            skLineSegment(sketch, "E8.6.0.38", {"start": v(-30.58, 44.35) * mm, "end": v(-30.58, 44.85) * mm});
            skLineSegment(sketch, "E8.9.0.38", {"start": v(-20.22, 44.35) * mm, "end": v(-20.22, 44.85) * mm});
            skLineSegment(sketch, "E8.0.0.39", {"start": v(-30.58, 45.35) * mm, "end": v(-20.22, 45.35) * mm});
            skLineSegment(sketch, "E8.3.0.39", {"start": v(-30.58, 45.85) * mm, "end": v(-20.22, 45.85) * mm});
            skLineSegment(sketch, "E8.6.0.39", {"start": v(-30.58, 45.35) * mm, "end": v(-30.58, 45.85) * mm});
            skLineSegment(sketch, "E8.9.0.39", {"start": v(-20.22, 45.35) * mm, "end": v(-20.22, 45.85) * mm});
            skLineSegment(sketch, "E8.0.0.40", {"start": v(-30.58, 46.35) * mm, "end": v(-20.22, 46.35) * mm});
            skLineSegment(sketch, "E8.3.0.40", {"start": v(-30.58, 46.85) * mm, "end": v(-20.22, 46.85) * mm});
            skLineSegment(sketch, "E8.6.0.40", {"start": v(-30.58, 46.35) * mm, "end": v(-30.58, 46.85) * mm});
            skLineSegment(sketch, "E8.9.0.40", {"start": v(-20.22, 46.35) * mm, "end": v(-20.22, 46.85) * mm});
            skLineSegment(sketch, "E8.0.0.41", {"start": v(-30.58, 47.35) * mm, "end": v(-20.22, 47.35) * mm});
            skLineSegment(sketch, "E8.3.0.41", {"start": v(-30.58, 47.85) * mm, "end": v(-20.22, 47.85) * mm});
            skLineSegment(sketch, "E8.6.0.41", {"start": v(-30.58, 47.35) * mm, "end": v(-30.58, 47.85) * mm});
            skLineSegment(sketch, "E8.9.0.41", {"start": v(-20.22, 47.35) * mm, "end": v(-20.22, 47.85) * mm});
            skLineSegment(sketch, "E8.0.0.42", {"start": v(-30.58, 48.35) * mm, "end": v(-20.22, 48.35) * mm});
            skLineSegment(sketch, "E8.3.0.42", {"start": v(-30.58, 48.85) * mm, "end": v(-20.22, 48.85) * mm});
            skLineSegment(sketch, "E8.6.0.42", {"start": v(-30.58, 48.35) * mm, "end": v(-30.58, 48.85) * mm});
            skLineSegment(sketch, "E8.9.0.42", {"start": v(-20.22, 48.35) * mm, "end": v(-20.22, 48.85) * mm});
            skLineSegment(sketch, "E8.0.0.43", {"start": v(-30.58, 49.35) * mm, "end": v(-20.22, 49.35) * mm});
            skLineSegment(sketch, "E8.3.0.43", {"start": v(-30.58, 49.85) * mm, "end": v(-20.22, 49.85) * mm});
            skLineSegment(sketch, "E8.6.0.43", {"start": v(-30.58, 49.35) * mm, "end": v(-30.58, 49.85) * mm});
            skLineSegment(sketch, "E8.9.0.43", {"start": v(-20.22, 49.35) * mm, "end": v(-20.22, 49.85) * mm});
            skLineSegment(sketch, "E8.0.0.44", {"start": v(-30.58, 50.35) * mm, "end": v(-20.22, 50.35) * mm});
            skLineSegment(sketch, "E8.3.0.44", {"start": v(-30.58, 50.85) * mm, "end": v(-20.22, 50.85) * mm});
            skLineSegment(sketch, "E8.6.0.44", {"start": v(-30.58, 50.35) * mm, "end": v(-30.58, 50.85) * mm});
            skLineSegment(sketch, "E8.9.0.44", {"start": v(-20.22, 50.35) * mm, "end": v(-20.22, 50.85) * mm});
            skLineSegment(sketch, "E8.0.0.45", {"start": v(-30.58, 51.35) * mm, "end": v(-20.22, 51.35) * mm});
            skLineSegment(sketch, "E8.3.0.45", {"start": v(-30.58, 51.85) * mm, "end": v(-20.22, 51.85) * mm});
            skLineSegment(sketch, "E8.6.0.45", {"start": v(-30.58, 51.35) * mm, "end": v(-30.58, 51.85) * mm});
            skLineSegment(sketch, "E8.9.0.45", {"start": v(-20.22, 51.35) * mm, "end": v(-20.22, 51.85) * mm});
            skLineSegment(sketch, "E8.0.0.46", {"start": v(-30.58, 52.35) * mm, "end": v(-20.22, 52.35) * mm});
            skLineSegment(sketch, "E8.3.0.46", {"start": v(-30.58, 52.85) * mm, "end": v(-20.22, 52.85) * mm});
            skLineSegment(sketch, "E8.6.0.46", {"start": v(-30.58, 52.35) * mm, "end": v(-30.58, 52.85) * mm});
            skLineSegment(sketch, "E8.9.0.46", {"start": v(-20.22, 52.35) * mm, "end": v(-20.22, 52.85) * mm});
            skLineSegment(sketch, "E8.0.0.47", {"start": v(-30.58, 53.35) * mm, "end": v(-20.22, 53.35) * mm});
            skLineSegment(sketch, "E8.3.0.47", {"start": v(-30.58, 53.85) * mm, "end": v(-20.22, 53.85) * mm});
            skLineSegment(sketch, "E8.6.0.47", {"start": v(-30.58, 53.35) * mm, "end": v(-30.58, 53.85) * mm});
            skLineSegment(sketch, "E8.9.0.47", {"start": v(-20.22, 53.35) * mm, "end": v(-20.22, 53.85) * mm});
            skLineSegment(sketch, "E8.0.0.48", {"start": v(-30.58, 54.35) * mm, "end": v(-20.22, 54.35) * mm});
            skLineSegment(sketch, "E8.3.0.48", {"start": v(-30.58, 54.85) * mm, "end": v(-20.22, 54.85) * mm});
            skLineSegment(sketch, "E8.6.0.48", {"start": v(-30.58, 54.35) * mm, "end": v(-30.58, 54.85) * mm});
            skLineSegment(sketch, "E8.9.0.48", {"start": v(-20.22, 54.35) * mm, "end": v(-20.22, 54.85) * mm});
            skLineSegment(sketch, "E8.0.0.49", {"start": v(-30.58, 55.35) * mm, "end": v(-20.22, 55.35) * mm});
            skLineSegment(sketch, "E8.3.0.49", {"start": v(-30.58, 55.85) * mm, "end": v(-20.22, 55.85) * mm});
            skLineSegment(sketch, "E8.6.0.49", {"start": v(-30.58, 55.35) * mm, "end": v(-30.58, 55.85) * mm});
            skLineSegment(sketch, "E8.9.0.49", {"start": v(-20.22, 55.35) * mm, "end": v(-20.22, 55.85) * mm});
            skLineSegment(sketch, "E8.0.0.50", {"start": v(-30.58, 56.35) * mm, "end": v(-20.22, 56.35) * mm});
            skLineSegment(sketch, "E8.3.0.50", {"start": v(-30.58, 56.85) * mm, "end": v(-20.22, 56.85) * mm});
            skLineSegment(sketch, "E8.6.0.50", {"start": v(-30.58, 56.35) * mm, "end": v(-30.58, 56.85) * mm});
            skLineSegment(sketch, "E8.9.0.50", {"start": v(-20.22, 56.35) * mm, "end": v(-20.22, 56.85) * mm});
            skLineSegment(sketch, "E8.0.0.51", {"start": v(-30.58, 57.35) * mm, "end": v(-20.22, 57.35) * mm});
            skLineSegment(sketch, "E8.3.0.51", {"start": v(-30.58, 57.85) * mm, "end": v(-20.22, 57.85) * mm});
            skLineSegment(sketch, "E8.6.0.51", {"start": v(-30.58, 57.35) * mm, "end": v(-30.58, 57.85) * mm});
            skLineSegment(sketch, "E8.9.0.51", {"start": v(-20.22, 57.35) * mm, "end": v(-20.22, 57.85) * mm});
            skLineSegment(sketch, "E8.0.0.52", {"start": v(-30.58, 58.35) * mm, "end": v(-20.22, 58.35) * mm});
            skLineSegment(sketch, "E8.3.0.52", {"start": v(-30.58, 58.85) * mm, "end": v(-20.22, 58.85) * mm});
            skLineSegment(sketch, "E8.6.0.52", {"start": v(-30.58, 58.35) * mm, "end": v(-30.58, 58.85) * mm});
            skLineSegment(sketch, "E8.9.0.52", {"start": v(-20.22, 58.35) * mm, "end": v(-20.22, 58.85) * mm});
            skLineSegment(sketch, "E8.0.0.53", {"start": v(-30.58, 59.35) * mm, "end": v(-20.22, 59.35) * mm});
            skLineSegment(sketch, "E8.3.0.53", {"start": v(-30.58, 59.85) * mm, "end": v(-20.22, 59.85) * mm});
            skLineSegment(sketch, "E8.6.0.53", {"start": v(-30.58, 59.35) * mm, "end": v(-30.58, 59.85) * mm});
            skLineSegment(sketch, "E8.9.0.53", {"start": v(-20.22, 59.35) * mm, "end": v(-20.22, 59.85) * mm});
            skLineSegment(sketch, "E8.0.0.54", {"start": v(-30.58, 60.35) * mm, "end": v(-20.22, 60.35) * mm});
            skLineSegment(sketch, "E8.3.0.54", {"start": v(-30.58, 60.85) * mm, "end": v(-20.22, 60.85) * mm});
            skLineSegment(sketch, "E8.6.0.54", {"start": v(-30.58, 60.35) * mm, "end": v(-30.58, 60.85) * mm});
            skLineSegment(sketch, "E8.9.0.54", {"start": v(-20.22, 60.35) * mm, "end": v(-20.22, 60.85) * mm});
            skLineSegment(sketch, "E8.0.0.55", {"start": v(-30.58, 61.35) * mm, "end": v(-20.22, 61.35) * mm});
            skLineSegment(sketch, "E8.3.0.55", {"start": v(-30.58, 61.85) * mm, "end": v(-20.22, 61.85) * mm});
            skLineSegment(sketch, "E8.6.0.55", {"start": v(-30.58, 61.35) * mm, "end": v(-30.58, 61.85) * mm});
            skLineSegment(sketch, "E8.9.0.55", {"start": v(-20.22, 61.35) * mm, "end": v(-20.22, 61.85) * mm});
            skLineSegment(sketch, "E8.0.0.56", {"start": v(-30.58, 62.35) * mm, "end": v(-20.22, 62.35) * mm});
            skLineSegment(sketch, "E8.3.0.56", {"start": v(-30.58, 62.85) * mm, "end": v(-20.22, 62.85) * mm});
            skLineSegment(sketch, "E8.6.0.56", {"start": v(-30.58, 62.35) * mm, "end": v(-30.58, 62.85) * mm});
            skLineSegment(sketch, "E8.9.0.56", {"start": v(-20.22, 62.35) * mm, "end": v(-20.22, 62.85) * mm});
            skLineSegment(sketch, "E8.0.0.57", {"start": v(-30.58, 63.35) * mm, "end": v(-20.22, 63.35) * mm});
            skLineSegment(sketch, "E8.3.0.57", {"start": v(-30.58, 63.85) * mm, "end": v(-20.22, 63.85) * mm});
            skLineSegment(sketch, "E8.6.0.57", {"start": v(-30.58, 63.35) * mm, "end": v(-30.58, 63.85) * mm});
            skLineSegment(sketch, "E8.9.0.57", {"start": v(-20.22, 63.35) * mm, "end": v(-20.22, 63.85) * mm});
            skLineSegment(sketch, "E8.0.0.58", {"start": v(-30.58, 64.35) * mm, "end": v(-20.22, 64.35) * mm});
            skLineSegment(sketch, "E8.3.0.58", {"start": v(-30.58, 64.85) * mm, "end": v(-20.22, 64.85) * mm});
            skLineSegment(sketch, "E8.6.0.58", {"start": v(-30.58, 64.35) * mm, "end": v(-30.58, 64.85) * mm});
            skLineSegment(sketch, "E8.9.0.58", {"start": v(-20.22, 64.35) * mm, "end": v(-20.22, 64.85) * mm});
            skLineSegment(sketch, "E8.0.0.59", {"start": v(-30.58, 65.35) * mm, "end": v(-20.22, 65.35) * mm});
            skLineSegment(sketch, "E8.3.0.59", {"start": v(-30.58, 65.85) * mm, "end": v(-20.22, 65.85) * mm});
            skLineSegment(sketch, "E8.6.0.59", {"start": v(-30.58, 65.35) * mm, "end": v(-30.58, 65.85) * mm});
            skLineSegment(sketch, "E8.9.0.59", {"start": v(-20.22, 65.35) * mm, "end": v(-20.22, 65.85) * mm});
            skLineSegment(sketch, "E8.0.0.60", {"start": v(-30.58, 66.35) * mm, "end": v(-20.22, 66.35) * mm});
            skLineSegment(sketch, "E8.3.0.60", {"start": v(-30.58, 66.85) * mm, "end": v(-20.22, 66.85) * mm});
            skLineSegment(sketch, "E8.6.0.60", {"start": v(-30.58, 66.35) * mm, "end": v(-30.58, 66.85) * mm});
            skLineSegment(sketch, "E8.9.0.60", {"start": v(-20.22, 66.35) * mm, "end": v(-20.22, 66.85) * mm});
            skLineSegment(sketch, "E8.0.0.61", {"start": v(-30.58, 67.35) * mm, "end": v(-20.22, 67.35) * mm});
            skLineSegment(sketch, "E8.3.0.61", {"start": v(-30.58, 67.85) * mm, "end": v(-20.22, 67.85) * mm});
            skLineSegment(sketch, "E8.6.0.61", {"start": v(-30.58, 67.35) * mm, "end": v(-30.58, 67.85) * mm});
            skLineSegment(sketch, "E8.9.0.61", {"start": v(-20.22, 67.35) * mm, "end": v(-20.22, 67.85) * mm});
            skLineSegment(sketch, "E8.0.0.62", {"start": v(-30.58, 68.35) * mm, "end": v(-20.22, 68.35) * mm});
            skLineSegment(sketch, "E8.3.0.62", {"start": v(-30.58, 68.85) * mm, "end": v(-20.22, 68.85) * mm});
            skLineSegment(sketch, "E8.6.0.62", {"start": v(-30.58, 68.35) * mm, "end": v(-30.58, 68.85) * mm});
            skLineSegment(sketch, "E8.9.0.62", {"start": v(-20.22, 68.35) * mm, "end": v(-20.22, 68.85) * mm});
            skLineSegment(sketch, "E8.0.0.63", {"start": v(-30.58, 69.35) * mm, "end": v(-20.22, 69.35) * mm});
            skLineSegment(sketch, "E8.3.0.63", {"start": v(-30.58, 69.85) * mm, "end": v(-20.22, 69.85) * mm});
            skLineSegment(sketch, "E8.6.0.63", {"start": v(-30.58, 69.35) * mm, "end": v(-30.58, 69.85) * mm});
            skLineSegment(sketch, "E8.9.0.63", {"start": v(-20.22, 69.35) * mm, "end": v(-20.22, 69.85) * mm});
            skLineSegment(sketch, "E8.0.0.64", {"start": v(-30.58, 70.35) * mm, "end": v(-20.22, 70.35) * mm});
            skLineSegment(sketch, "E8.3.0.64", {"start": v(-30.58, 70.85) * mm, "end": v(-20.22, 70.85) * mm});
            skLineSegment(sketch, "E8.6.0.64", {"start": v(-30.58, 70.35) * mm, "end": v(-30.58, 70.85) * mm});
            skLineSegment(sketch, "E8.9.0.64", {"start": v(-20.22, 70.35) * mm, "end": v(-20.22, 70.85) * mm});
            skLineSegment(sketch, "E8.0.0.65", {"start": v(-30.58, 71.35) * mm, "end": v(-20.22, 71.35) * mm});
            skLineSegment(sketch, "E8.3.0.65", {"start": v(-30.58, 71.85) * mm, "end": v(-20.22, 71.85) * mm});
            skLineSegment(sketch, "E8.6.0.65", {"start": v(-30.58, 71.35) * mm, "end": v(-30.58, 71.85) * mm});
            skLineSegment(sketch, "E8.9.0.65", {"start": v(-20.22, 71.35) * mm, "end": v(-20.22, 71.85) * mm});
            skLineSegment(sketch, "E8.0.0.66", {"start": v(-30.58, 72.35) * mm, "end": v(-20.22, 72.35) * mm});
            skLineSegment(sketch, "E8.3.0.66", {"start": v(-30.58, 72.85) * mm, "end": v(-20.22, 72.85) * mm});
            skLineSegment(sketch, "E8.6.0.66", {"start": v(-30.58, 72.35) * mm, "end": v(-30.58, 72.85) * mm});
            skLineSegment(sketch, "E8.9.0.66", {"start": v(-20.22, 72.35) * mm, "end": v(-20.22, 72.85) * mm});
            skLineSegment(sketch, "E8.0.0.67", {"start": v(-30.58, 73.35) * mm, "end": v(-20.22, 73.35) * mm});
            skLineSegment(sketch, "E8.3.0.67", {"start": v(-30.58, 73.85) * mm, "end": v(-20.22, 73.85) * mm});
            skLineSegment(sketch, "E8.6.0.67", {"start": v(-30.58, 73.35) * mm, "end": v(-30.58, 73.85) * mm});
            skLineSegment(sketch, "E8.9.0.67", {"start": v(-20.22, 73.35) * mm, "end": v(-20.22, 73.85) * mm});
            skLineSegment(sketch, "E8.0.0.68", {"start": v(-30.58, 74.35) * mm, "end": v(-20.22, 74.35) * mm});
            skLineSegment(sketch, "E8.3.0.68", {"start": v(-30.58, 74.85) * mm, "end": v(-20.22, 74.85) * mm});
            skLineSegment(sketch, "E8.6.0.68", {"start": v(-30.58, 74.35) * mm, "end": v(-30.58, 74.85) * mm});
            skLineSegment(sketch, "E8.9.0.68", {"start": v(-20.22, 74.35) * mm, "end": v(-20.22, 74.85) * mm});
            skLineSegment(sketch, "E8.0.1.18", {"start": v(-5.18, 24.35) * mm, "end": v(5.18, 24.35) * mm});
            skLineSegment(sketch, "E8.3.1.18", {"start": v(-5.18, 24.85) * mm, "end": v(5.18, 24.85) * mm});
            skLineSegment(sketch, "E8.6.1.18", {"start": v(-5.18, 24.35) * mm, "end": v(-5.18, 24.85) * mm});
            skLineSegment(sketch, "E8.9.1.18", {"start": v(5.18, 24.35) * mm, "end": v(5.18, 24.85) * mm});
            skLineSegment(sketch, "E8.0.1.19", {"start": v(-5.18, 25.35) * mm, "end": v(5.18, 25.35) * mm});
            skLineSegment(sketch, "E8.3.1.19", {"start": v(-5.18, 25.85) * mm, "end": v(5.18, 25.85) * mm});
            skLineSegment(sketch, "E8.6.1.19", {"start": v(-5.18, 25.35) * mm, "end": v(-5.18, 25.85) * mm});
            skLineSegment(sketch, "E8.9.1.19", {"start": v(5.18, 25.35) * mm, "end": v(5.18, 25.85) * mm});
            skLineSegment(sketch, "E8.0.1.20", {"start": v(-5.18, 26.35) * mm, "end": v(5.18, 26.35) * mm});
            skLineSegment(sketch, "E8.3.1.20", {"start": v(-5.18, 26.85) * mm, "end": v(5.18, 26.85) * mm});
            skLineSegment(sketch, "E8.6.1.20", {"start": v(-5.18, 26.35) * mm, "end": v(-5.18, 26.85) * mm});
            skLineSegment(sketch, "E8.9.1.20", {"start": v(5.18, 26.35) * mm, "end": v(5.18, 26.85) * mm});
            skLineSegment(sketch, "E8.0.1.21", {"start": v(-5.18, 27.35) * mm, "end": v(5.18, 27.35) * mm});
            skLineSegment(sketch, "E8.3.1.21", {"start": v(-5.18, 27.85) * mm, "end": v(5.18, 27.85) * mm});
            skLineSegment(sketch, "E8.6.1.21", {"start": v(-5.18, 27.35) * mm, "end": v(-5.18, 27.85) * mm});
            skLineSegment(sketch, "E8.9.1.21", {"start": v(5.18, 27.35) * mm, "end": v(5.18, 27.85) * mm});
            skLineSegment(sketch, "E8.0.1.22", {"start": v(-5.18, 28.35) * mm, "end": v(5.18, 28.35) * mm});
            skLineSegment(sketch, "E8.3.1.22", {"start": v(-5.18, 28.85) * mm, "end": v(5.18, 28.85) * mm});
            skLineSegment(sketch, "E8.6.1.22", {"start": v(-5.18, 28.35) * mm, "end": v(-5.18, 28.85) * mm});
            skLineSegment(sketch, "E8.9.1.22", {"start": v(5.18, 28.35) * mm, "end": v(5.18, 28.85) * mm});
            skLineSegment(sketch, "E8.0.1.23", {"start": v(-5.18, 29.35) * mm, "end": v(5.18, 29.35) * mm});
            skLineSegment(sketch, "E8.3.1.23", {"start": v(-5.18, 29.85) * mm, "end": v(5.18, 29.85) * mm});
            skLineSegment(sketch, "E8.6.1.23", {"start": v(-5.18, 29.35) * mm, "end": v(-5.18, 29.85) * mm});
            skLineSegment(sketch, "E8.9.1.23", {"start": v(5.18, 29.35) * mm, "end": v(5.18, 29.85) * mm});
            skLineSegment(sketch, "E8.0.1.24", {"start": v(-5.18, 30.35) * mm, "end": v(5.18, 30.35) * mm});
            skLineSegment(sketch, "E8.3.1.24", {"start": v(-5.18, 30.85) * mm, "end": v(5.18, 30.85) * mm});
            skLineSegment(sketch, "E8.6.1.24", {"start": v(-5.18, 30.35) * mm, "end": v(-5.18, 30.85) * mm});
            skLineSegment(sketch, "E8.9.1.24", {"start": v(5.18, 30.35) * mm, "end": v(5.18, 30.85) * mm});
            skLineSegment(sketch, "E8.0.1.25", {"start": v(-5.18, 31.35) * mm, "end": v(5.18, 31.35) * mm});
            skLineSegment(sketch, "E8.3.1.25", {"start": v(-5.18, 31.85) * mm, "end": v(5.18, 31.85) * mm});
            skLineSegment(sketch, "E8.6.1.25", {"start": v(-5.18, 31.35) * mm, "end": v(-5.18, 31.85) * mm});
            skLineSegment(sketch, "E8.9.1.25", {"start": v(5.18, 31.35) * mm, "end": v(5.18, 31.85) * mm});
            skLineSegment(sketch, "E8.0.1.26", {"start": v(-5.18, 32.35) * mm, "end": v(5.18, 32.35) * mm});
            skLineSegment(sketch, "E8.3.1.26", {"start": v(-5.18, 32.85) * mm, "end": v(5.18, 32.85) * mm});
            skLineSegment(sketch, "E8.6.1.26", {"start": v(-5.18, 32.35) * mm, "end": v(-5.18, 32.85) * mm});
            skLineSegment(sketch, "E8.9.1.26", {"start": v(5.18, 32.35) * mm, "end": v(5.18, 32.85) * mm});
            skLineSegment(sketch, "E8.0.1.27", {"start": v(-5.18, 33.35) * mm, "end": v(5.18, 33.35) * mm});
            skLineSegment(sketch, "E8.3.1.27", {"start": v(-5.18, 33.85) * mm, "end": v(5.18, 33.85) * mm});
            skLineSegment(sketch, "E8.6.1.27", {"start": v(-5.18, 33.35) * mm, "end": v(-5.18, 33.85) * mm});
            skLineSegment(sketch, "E8.9.1.27", {"start": v(5.18, 33.35) * mm, "end": v(5.18, 33.85) * mm});
            skLineSegment(sketch, "E8.0.1.28", {"start": v(-5.18, 34.35) * mm, "end": v(5.18, 34.35) * mm});
            skLineSegment(sketch, "E8.3.1.28", {"start": v(-5.18, 34.85) * mm, "end": v(5.18, 34.85) * mm});
            skLineSegment(sketch, "E8.6.1.28", {"start": v(-5.18, 34.35) * mm, "end": v(-5.18, 34.85) * mm});
            skLineSegment(sketch, "E8.9.1.28", {"start": v(5.18, 34.35) * mm, "end": v(5.18, 34.85) * mm});
            skLineSegment(sketch, "E8.0.1.29", {"start": v(-5.18, 35.35) * mm, "end": v(5.18, 35.35) * mm});
            skLineSegment(sketch, "E8.3.1.29", {"start": v(-5.18, 35.85) * mm, "end": v(5.18, 35.85) * mm});
            skLineSegment(sketch, "E8.6.1.29", {"start": v(-5.18, 35.35) * mm, "end": v(-5.18, 35.85) * mm});
            skLineSegment(sketch, "E8.9.1.29", {"start": v(5.18, 35.35) * mm, "end": v(5.18, 35.85) * mm});
            skLineSegment(sketch, "E8.0.1.30", {"start": v(-5.18, 36.35) * mm, "end": v(5.18, 36.35) * mm});
            skLineSegment(sketch, "E8.3.1.30", {"start": v(-5.18, 36.85) * mm, "end": v(5.18, 36.85) * mm});
            skLineSegment(sketch, "E8.6.1.30", {"start": v(-5.18, 36.35) * mm, "end": v(-5.18, 36.85) * mm});
            skLineSegment(sketch, "E8.9.1.30", {"start": v(5.18, 36.35) * mm, "end": v(5.18, 36.85) * mm});
            skLineSegment(sketch, "E8.0.1.31", {"start": v(-5.18, 37.35) * mm, "end": v(5.18, 37.35) * mm});
            skLineSegment(sketch, "E8.3.1.31", {"start": v(-5.18, 37.85) * mm, "end": v(5.18, 37.85) * mm});
            skLineSegment(sketch, "E8.6.1.31", {"start": v(-5.18, 37.35) * mm, "end": v(-5.18, 37.85) * mm});
            skLineSegment(sketch, "E8.9.1.31", {"start": v(5.18, 37.35) * mm, "end": v(5.18, 37.85) * mm});
            skLineSegment(sketch, "E8.0.1.32", {"start": v(-5.18, 38.35) * mm, "end": v(5.18, 38.35) * mm});
            skLineSegment(sketch, "E8.3.1.32", {"start": v(-5.18, 38.85) * mm, "end": v(5.18, 38.85) * mm});
            skLineSegment(sketch, "E8.6.1.32", {"start": v(-5.18, 38.35) * mm, "end": v(-5.18, 38.85) * mm});
            skLineSegment(sketch, "E8.9.1.32", {"start": v(5.18, 38.35) * mm, "end": v(5.18, 38.85) * mm});
            skLineSegment(sketch, "E8.0.1.33", {"start": v(-5.18, 39.35) * mm, "end": v(5.18, 39.35) * mm});
            skLineSegment(sketch, "E8.3.1.33", {"start": v(-5.18, 39.85) * mm, "end": v(5.18, 39.85) * mm});
            skLineSegment(sketch, "E8.6.1.33", {"start": v(-5.18, 39.35) * mm, "end": v(-5.18, 39.85) * mm});
            skLineSegment(sketch, "E8.9.1.33", {"start": v(5.18, 39.35) * mm, "end": v(5.18, 39.85) * mm});
            skLineSegment(sketch, "E8.0.1.34", {"start": v(-5.18, 40.35) * mm, "end": v(5.18, 40.35) * mm});
            skLineSegment(sketch, "E8.3.1.34", {"start": v(-5.18, 40.85) * mm, "end": v(5.18, 40.85) * mm});
            skLineSegment(sketch, "E8.6.1.34", {"start": v(-5.18, 40.35) * mm, "end": v(-5.18, 40.85) * mm});
            skLineSegment(sketch, "E8.9.1.34", {"start": v(5.18, 40.35) * mm, "end": v(5.18, 40.85) * mm});
            skLineSegment(sketch, "E8.0.1.35", {"start": v(-5.18, 41.35) * mm, "end": v(5.18, 41.35) * mm});
            skLineSegment(sketch, "E8.3.1.35", {"start": v(-5.18, 41.85) * mm, "end": v(5.18, 41.85) * mm});
            skLineSegment(sketch, "E8.6.1.35", {"start": v(-5.18, 41.35) * mm, "end": v(-5.18, 41.85) * mm});
            skLineSegment(sketch, "E8.9.1.35", {"start": v(5.18, 41.35) * mm, "end": v(5.18, 41.85) * mm});
            skLineSegment(sketch, "E8.0.1.36", {"start": v(-5.18, 42.35) * mm, "end": v(5.18, 42.35) * mm});
            skLineSegment(sketch, "E8.3.1.36", {"start": v(-5.18, 42.85) * mm, "end": v(5.18, 42.85) * mm});
            skLineSegment(sketch, "E8.6.1.36", {"start": v(-5.18, 42.35) * mm, "end": v(-5.18, 42.85) * mm});
            skLineSegment(sketch, "E8.9.1.36", {"start": v(5.18, 42.35) * mm, "end": v(5.18, 42.85) * mm});
            skLineSegment(sketch, "E8.0.1.37", {"start": v(-5.18, 43.35) * mm, "end": v(5.18, 43.35) * mm});
            skLineSegment(sketch, "E8.3.1.37", {"start": v(-5.18, 43.85) * mm, "end": v(5.18, 43.85) * mm});
            skLineSegment(sketch, "E8.6.1.37", {"start": v(-5.18, 43.35) * mm, "end": v(-5.18, 43.85) * mm});
            skLineSegment(sketch, "E8.9.1.37", {"start": v(5.18, 43.35) * mm, "end": v(5.18, 43.85) * mm});
            skLineSegment(sketch, "E8.0.1.38", {"start": v(-5.18, 44.35) * mm, "end": v(5.18, 44.35) * mm});
            skLineSegment(sketch, "E8.3.1.38", {"start": v(-5.18, 44.85) * mm, "end": v(5.18, 44.85) * mm});
            skLineSegment(sketch, "E8.6.1.38", {"start": v(-5.18, 44.35) * mm, "end": v(-5.18, 44.85) * mm});
            skLineSegment(sketch, "E8.9.1.38", {"start": v(5.18, 44.35) * mm, "end": v(5.18, 44.85) * mm});
            skLineSegment(sketch, "E8.0.1.39", {"start": v(-5.18, 45.35) * mm, "end": v(5.18, 45.35) * mm});
            skLineSegment(sketch, "E8.3.1.39", {"start": v(-5.18, 45.85) * mm, "end": v(5.18, 45.85) * mm});
            skLineSegment(sketch, "E8.6.1.39", {"start": v(-5.18, 45.35) * mm, "end": v(-5.18, 45.85) * mm});
            skLineSegment(sketch, "E8.9.1.39", {"start": v(5.18, 45.35) * mm, "end": v(5.18, 45.85) * mm});
            skLineSegment(sketch, "E8.0.1.40", {"start": v(-5.18, 46.35) * mm, "end": v(5.18, 46.35) * mm});
            skLineSegment(sketch, "E8.3.1.40", {"start": v(-5.18, 46.85) * mm, "end": v(5.18, 46.85) * mm});
            skLineSegment(sketch, "E8.6.1.40", {"start": v(-5.18, 46.35) * mm, "end": v(-5.18, 46.85) * mm});
            skLineSegment(sketch, "E8.9.1.40", {"start": v(5.18, 46.35) * mm, "end": v(5.18, 46.85) * mm});
            skLineSegment(sketch, "E8.0.1.41", {"start": v(-5.18, 47.35) * mm, "end": v(5.18, 47.35) * mm});
            skLineSegment(sketch, "E8.3.1.41", {"start": v(-5.18, 47.85) * mm, "end": v(5.18, 47.85) * mm});
            skLineSegment(sketch, "E8.6.1.41", {"start": v(-5.18, 47.35) * mm, "end": v(-5.18, 47.85) * mm});
            skLineSegment(sketch, "E8.9.1.41", {"start": v(5.18, 47.35) * mm, "end": v(5.18, 47.85) * mm});
            skLineSegment(sketch, "E8.0.1.42", {"start": v(-5.18, 48.35) * mm, "end": v(5.18, 48.35) * mm});
            skLineSegment(sketch, "E8.3.1.42", {"start": v(-5.18, 48.85) * mm, "end": v(5.18, 48.85) * mm});
            skLineSegment(sketch, "E8.6.1.42", {"start": v(-5.18, 48.35) * mm, "end": v(-5.18, 48.85) * mm});
            skLineSegment(sketch, "E8.9.1.42", {"start": v(5.18, 48.35) * mm, "end": v(5.18, 48.85) * mm});
            skLineSegment(sketch, "E8.0.1.43", {"start": v(-5.18, 49.35) * mm, "end": v(5.18, 49.35) * mm});
            skLineSegment(sketch, "E8.3.1.43", {"start": v(-5.18, 49.85) * mm, "end": v(5.18, 49.85) * mm});
            skLineSegment(sketch, "E8.6.1.43", {"start": v(-5.18, 49.35) * mm, "end": v(-5.18, 49.85) * mm});
            skLineSegment(sketch, "E8.9.1.43", {"start": v(5.18, 49.35) * mm, "end": v(5.18, 49.85) * mm});
            skLineSegment(sketch, "E8.0.1.44", {"start": v(-5.18, 50.35) * mm, "end": v(5.18, 50.35) * mm});
            skLineSegment(sketch, "E8.3.1.44", {"start": v(-5.18, 50.85) * mm, "end": v(5.18, 50.85) * mm});
            skLineSegment(sketch, "E8.6.1.44", {"start": v(-5.18, 50.35) * mm, "end": v(-5.18, 50.85) * mm});
            skLineSegment(sketch, "E8.9.1.44", {"start": v(5.18, 50.35) * mm, "end": v(5.18, 50.85) * mm});
            skLineSegment(sketch, "E8.0.1.45", {"start": v(-5.18, 51.35) * mm, "end": v(5.18, 51.35) * mm});
            skLineSegment(sketch, "E8.3.1.45", {"start": v(-5.18, 51.85) * mm, "end": v(5.18, 51.85) * mm});
            skLineSegment(sketch, "E8.6.1.45", {"start": v(-5.18, 51.35) * mm, "end": v(-5.18, 51.85) * mm});
            skLineSegment(sketch, "E8.9.1.45", {"start": v(5.18, 51.35) * mm, "end": v(5.18, 51.85) * mm});
            skLineSegment(sketch, "E8.0.1.46", {"start": v(-5.18, 52.35) * mm, "end": v(5.18, 52.35) * mm});
            skLineSegment(sketch, "E8.3.1.46", {"start": v(-5.18, 52.85) * mm, "end": v(5.18, 52.85) * mm});
            skLineSegment(sketch, "E8.6.1.46", {"start": v(-5.18, 52.35) * mm, "end": v(-5.18, 52.85) * mm});
            skLineSegment(sketch, "E8.9.1.46", {"start": v(5.18, 52.35) * mm, "end": v(5.18, 52.85) * mm});
            skLineSegment(sketch, "E8.0.1.47", {"start": v(-5.18, 53.35) * mm, "end": v(5.18, 53.35) * mm});
            skLineSegment(sketch, "E8.3.1.47", {"start": v(-5.18, 53.85) * mm, "end": v(5.18, 53.85) * mm});
            skLineSegment(sketch, "E8.6.1.47", {"start": v(-5.18, 53.35) * mm, "end": v(-5.18, 53.85) * mm});
            skLineSegment(sketch, "E8.9.1.47", {"start": v(5.18, 53.35) * mm, "end": v(5.18, 53.85) * mm});
            skLineSegment(sketch, "E8.0.1.48", {"start": v(-5.18, 54.35) * mm, "end": v(5.18, 54.35) * mm});
            skLineSegment(sketch, "E8.3.1.48", {"start": v(-5.18, 54.85) * mm, "end": v(5.18, 54.85) * mm});
            skLineSegment(sketch, "E8.6.1.48", {"start": v(-5.18, 54.35) * mm, "end": v(-5.18, 54.85) * mm});
            skLineSegment(sketch, "E8.9.1.48", {"start": v(5.18, 54.35) * mm, "end": v(5.18, 54.85) * mm});
            skLineSegment(sketch, "E8.0.1.49", {"start": v(-5.18, 55.35) * mm, "end": v(5.18, 55.35) * mm});
            skLineSegment(sketch, "E8.3.1.49", {"start": v(-5.18, 55.85) * mm, "end": v(5.18, 55.85) * mm});
            skLineSegment(sketch, "E8.6.1.49", {"start": v(-5.18, 55.35) * mm, "end": v(-5.18, 55.85) * mm});
            skLineSegment(sketch, "E8.9.1.49", {"start": v(5.18, 55.35) * mm, "end": v(5.18, 55.85) * mm});
            skLineSegment(sketch, "E8.0.1.50", {"start": v(-5.18, 56.35) * mm, "end": v(5.18, 56.35) * mm});
            skLineSegment(sketch, "E8.3.1.50", {"start": v(-5.18, 56.85) * mm, "end": v(5.18, 56.85) * mm});
            skLineSegment(sketch, "E8.6.1.50", {"start": v(-5.18, 56.35) * mm, "end": v(-5.18, 56.85) * mm});
            skLineSegment(sketch, "E8.9.1.50", {"start": v(5.18, 56.35) * mm, "end": v(5.18, 56.85) * mm});
            skLineSegment(sketch, "E8.0.1.51", {"start": v(-5.18, 57.35) * mm, "end": v(5.18, 57.35) * mm});
            skLineSegment(sketch, "E8.3.1.51", {"start": v(-5.18, 57.85) * mm, "end": v(5.18, 57.85) * mm});
            skLineSegment(sketch, "E8.6.1.51", {"start": v(-5.18, 57.35) * mm, "end": v(-5.18, 57.85) * mm});
            skLineSegment(sketch, "E8.9.1.51", {"start": v(5.18, 57.35) * mm, "end": v(5.18, 57.85) * mm});
            skLineSegment(sketch, "E8.0.1.52", {"start": v(-5.18, 58.35) * mm, "end": v(5.18, 58.35) * mm});
            skLineSegment(sketch, "E8.3.1.52", {"start": v(-5.18, 58.85) * mm, "end": v(5.18, 58.85) * mm});
            skLineSegment(sketch, "E8.6.1.52", {"start": v(-5.18, 58.35) * mm, "end": v(-5.18, 58.85) * mm});
            skLineSegment(sketch, "E8.9.1.52", {"start": v(5.18, 58.35) * mm, "end": v(5.18, 58.85) * mm});
            skLineSegment(sketch, "E8.0.1.53", {"start": v(-5.18, 59.35) * mm, "end": v(5.18, 59.35) * mm});
            skLineSegment(sketch, "E8.3.1.53", {"start": v(-5.18, 59.85) * mm, "end": v(5.18, 59.85) * mm});
            skLineSegment(sketch, "E8.6.1.53", {"start": v(-5.18, 59.35) * mm, "end": v(-5.18, 59.85) * mm});
            skLineSegment(sketch, "E8.9.1.53", {"start": v(5.18, 59.35) * mm, "end": v(5.18, 59.85) * mm});
            skLineSegment(sketch, "E8.0.1.54", {"start": v(-5.18, 60.35) * mm, "end": v(5.18, 60.35) * mm});
            skLineSegment(sketch, "E8.3.1.54", {"start": v(-5.18, 60.85) * mm, "end": v(5.18, 60.85) * mm});
            skLineSegment(sketch, "E8.6.1.54", {"start": v(-5.18, 60.35) * mm, "end": v(-5.18, 60.85) * mm});
            skLineSegment(sketch, "E8.9.1.54", {"start": v(5.18, 60.35) * mm, "end": v(5.18, 60.85) * mm});
            skLineSegment(sketch, "E8.0.1.55", {"start": v(-5.18, 61.35) * mm, "end": v(5.18, 61.35) * mm});
            skLineSegment(sketch, "E8.3.1.55", {"start": v(-5.18, 61.85) * mm, "end": v(5.18, 61.85) * mm});
            skLineSegment(sketch, "E8.6.1.55", {"start": v(-5.18, 61.35) * mm, "end": v(-5.18, 61.85) * mm});
            skLineSegment(sketch, "E8.9.1.55", {"start": v(5.18, 61.35) * mm, "end": v(5.18, 61.85) * mm});
            skLineSegment(sketch, "E8.0.1.56", {"start": v(-5.18, 62.35) * mm, "end": v(5.18, 62.35) * mm});
            skLineSegment(sketch, "E8.3.1.56", {"start": v(-5.18, 62.85) * mm, "end": v(5.18, 62.85) * mm});
            skLineSegment(sketch, "E8.6.1.56", {"start": v(-5.18, 62.35) * mm, "end": v(-5.18, 62.85) * mm});
            skLineSegment(sketch, "E8.9.1.56", {"start": v(5.18, 62.35) * mm, "end": v(5.18, 62.85) * mm});
            skLineSegment(sketch, "E8.0.1.57", {"start": v(-5.18, 63.35) * mm, "end": v(5.18, 63.35) * mm});
            skLineSegment(sketch, "E8.3.1.57", {"start": v(-5.18, 63.85) * mm, "end": v(5.18, 63.85) * mm});
            skLineSegment(sketch, "E8.6.1.57", {"start": v(-5.18, 63.35) * mm, "end": v(-5.18, 63.85) * mm});
            skLineSegment(sketch, "E8.9.1.57", {"start": v(5.18, 63.35) * mm, "end": v(5.18, 63.85) * mm});
            skLineSegment(sketch, "E8.0.1.58", {"start": v(-5.18, 64.35) * mm, "end": v(5.18, 64.35) * mm});
            skLineSegment(sketch, "E8.3.1.58", {"start": v(-5.18, 64.85) * mm, "end": v(5.18, 64.85) * mm});
            skLineSegment(sketch, "E8.6.1.58", {"start": v(-5.18, 64.35) * mm, "end": v(-5.18, 64.85) * mm});
            skLineSegment(sketch, "E8.9.1.58", {"start": v(5.18, 64.35) * mm, "end": v(5.18, 64.85) * mm});
            skLineSegment(sketch, "E8.0.1.59", {"start": v(-5.18, 65.35) * mm, "end": v(5.18, 65.35) * mm});
            skLineSegment(sketch, "E8.3.1.59", {"start": v(-5.18, 65.85) * mm, "end": v(5.18, 65.85) * mm});
            skLineSegment(sketch, "E8.6.1.59", {"start": v(-5.18, 65.35) * mm, "end": v(-5.18, 65.85) * mm});
            skLineSegment(sketch, "E8.9.1.59", {"start": v(5.18, 65.35) * mm, "end": v(5.18, 65.85) * mm});
            skLineSegment(sketch, "E8.0.1.60", {"start": v(-5.18, 66.35) * mm, "end": v(5.18, 66.35) * mm});
            skLineSegment(sketch, "E8.3.1.60", {"start": v(-5.18, 66.85) * mm, "end": v(5.18, 66.85) * mm});
            skLineSegment(sketch, "E8.6.1.60", {"start": v(-5.18, 66.35) * mm, "end": v(-5.18, 66.85) * mm});
            skLineSegment(sketch, "E8.9.1.60", {"start": v(5.18, 66.35) * mm, "end": v(5.18, 66.85) * mm});
            skLineSegment(sketch, "E8.0.1.61", {"start": v(-5.18, 67.35) * mm, "end": v(5.18, 67.35) * mm});
            skLineSegment(sketch, "E8.3.1.61", {"start": v(-5.18, 67.85) * mm, "end": v(5.18, 67.85) * mm});
            skLineSegment(sketch, "E8.6.1.61", {"start": v(-5.18, 67.35) * mm, "end": v(-5.18, 67.85) * mm});
            skLineSegment(sketch, "E8.9.1.61", {"start": v(5.18, 67.35) * mm, "end": v(5.18, 67.85) * mm});
            skLineSegment(sketch, "E8.0.1.62", {"start": v(-5.18, 68.35) * mm, "end": v(5.18, 68.35) * mm});
            skLineSegment(sketch, "E8.3.1.62", {"start": v(-5.18, 68.85) * mm, "end": v(5.18, 68.85) * mm});
            skLineSegment(sketch, "E8.6.1.62", {"start": v(-5.18, 68.35) * mm, "end": v(-5.18, 68.85) * mm});
            skLineSegment(sketch, "E8.9.1.62", {"start": v(5.18, 68.35) * mm, "end": v(5.18, 68.85) * mm});
            skLineSegment(sketch, "E8.0.1.63", {"start": v(-5.18, 69.35) * mm, "end": v(5.18, 69.35) * mm});
            skLineSegment(sketch, "E8.3.1.63", {"start": v(-5.18, 69.85) * mm, "end": v(5.18, 69.85) * mm});
            skLineSegment(sketch, "E8.6.1.63", {"start": v(-5.18, 69.35) * mm, "end": v(-5.18, 69.85) * mm});
            skLineSegment(sketch, "E8.9.1.63", {"start": v(5.18, 69.35) * mm, "end": v(5.18, 69.85) * mm});
            skLineSegment(sketch, "E8.0.1.64", {"start": v(-5.18, 70.35) * mm, "end": v(5.18, 70.35) * mm});
            skLineSegment(sketch, "E8.3.1.64", {"start": v(-5.18, 70.85) * mm, "end": v(5.18, 70.85) * mm});
            skLineSegment(sketch, "E8.6.1.64", {"start": v(-5.18, 70.35) * mm, "end": v(-5.18, 70.85) * mm});
            skLineSegment(sketch, "E8.9.1.64", {"start": v(5.18, 70.35) * mm, "end": v(5.18, 70.85) * mm});
            skLineSegment(sketch, "E8.0.1.65", {"start": v(-5.18, 71.35) * mm, "end": v(5.18, 71.35) * mm});
            skLineSegment(sketch, "E8.3.1.65", {"start": v(-5.18, 71.85) * mm, "end": v(5.18, 71.85) * mm});
            skLineSegment(sketch, "E8.6.1.65", {"start": v(-5.18, 71.35) * mm, "end": v(-5.18, 71.85) * mm});
            skLineSegment(sketch, "E8.9.1.65", {"start": v(5.18, 71.35) * mm, "end": v(5.18, 71.85) * mm});
            skLineSegment(sketch, "E8.0.1.66", {"start": v(-5.18, 72.35) * mm, "end": v(5.18, 72.35) * mm});
            skLineSegment(sketch, "E8.3.1.66", {"start": v(-5.18, 72.85) * mm, "end": v(5.18, 72.85) * mm});
            skLineSegment(sketch, "E8.6.1.66", {"start": v(-5.18, 72.35) * mm, "end": v(-5.18, 72.85) * mm});
            skLineSegment(sketch, "E8.9.1.66", {"start": v(5.18, 72.35) * mm, "end": v(5.18, 72.85) * mm});
            skLineSegment(sketch, "E8.0.1.67", {"start": v(-5.18, 73.35) * mm, "end": v(5.18, 73.35) * mm});
            skLineSegment(sketch, "E8.3.1.67", {"start": v(-5.18, 73.85) * mm, "end": v(5.18, 73.85) * mm});
            skLineSegment(sketch, "E8.6.1.67", {"start": v(-5.18, 73.35) * mm, "end": v(-5.18, 73.85) * mm});
            skLineSegment(sketch, "E8.9.1.67", {"start": v(5.18, 73.35) * mm, "end": v(5.18, 73.85) * mm});
            skLineSegment(sketch, "E8.0.1.68", {"start": v(-5.18, 74.35) * mm, "end": v(5.18, 74.35) * mm});
            skLineSegment(sketch, "E8.3.1.68", {"start": v(-5.18, 74.85) * mm, "end": v(5.18, 74.85) * mm});
            skLineSegment(sketch, "E8.6.1.68", {"start": v(-5.18, 74.35) * mm, "end": v(-5.18, 74.85) * mm});
            skLineSegment(sketch, "E8.9.1.68", {"start": v(5.18, 74.35) * mm, "end": v(5.18, 74.85) * mm});
            skLineSegment(sketch, "E8.0.2.18", {"start": v(20.22, 24.35) * mm, "end": v(30.58, 24.35) * mm});
            skLineSegment(sketch, "E8.3.2.18", {"start": v(20.22, 24.85) * mm, "end": v(30.58, 24.85) * mm});
            skLineSegment(sketch, "E8.6.2.18", {"start": v(20.22, 24.35) * mm, "end": v(20.22, 24.85) * mm});
            skLineSegment(sketch, "E8.9.2.18", {"start": v(30.58, 24.35) * mm, "end": v(30.58, 24.85) * mm});
            skLineSegment(sketch, "E8.0.2.19", {"start": v(20.22, 25.35) * mm, "end": v(30.58, 25.35) * mm});
            skLineSegment(sketch, "E8.3.2.19", {"start": v(20.22, 25.85) * mm, "end": v(30.58, 25.85) * mm});
            skLineSegment(sketch, "E8.6.2.19", {"start": v(20.22, 25.35) * mm, "end": v(20.22, 25.85) * mm});
            skLineSegment(sketch, "E8.9.2.19", {"start": v(30.58, 25.35) * mm, "end": v(30.58, 25.85) * mm});
            skLineSegment(sketch, "E8.0.2.20", {"start": v(20.22, 26.35) * mm, "end": v(30.58, 26.35) * mm});
            skLineSegment(sketch, "E8.3.2.20", {"start": v(20.22, 26.85) * mm, "end": v(30.58, 26.85) * mm});
            skLineSegment(sketch, "E8.6.2.20", {"start": v(20.22, 26.35) * mm, "end": v(20.22, 26.85) * mm});
            skLineSegment(sketch, "E8.9.2.20", {"start": v(30.58, 26.35) * mm, "end": v(30.58, 26.85) * mm});
            skLineSegment(sketch, "E8.0.2.21", {"start": v(20.22, 27.35) * mm, "end": v(30.58, 27.35) * mm});
            skLineSegment(sketch, "E8.3.2.21", {"start": v(20.22, 27.85) * mm, "end": v(30.58, 27.85) * mm});
            skLineSegment(sketch, "E8.6.2.21", {"start": v(20.22, 27.35) * mm, "end": v(20.22, 27.85) * mm});
            skLineSegment(sketch, "E8.9.2.21", {"start": v(30.58, 27.35) * mm, "end": v(30.58, 27.85) * mm});
            skLineSegment(sketch, "E8.0.2.22", {"start": v(20.22, 28.35) * mm, "end": v(30.58, 28.35) * mm});
            skLineSegment(sketch, "E8.3.2.22", {"start": v(20.22, 28.85) * mm, "end": v(30.58, 28.85) * mm});
            skLineSegment(sketch, "E8.6.2.22", {"start": v(20.22, 28.35) * mm, "end": v(20.22, 28.85) * mm});
            skLineSegment(sketch, "E8.9.2.22", {"start": v(30.58, 28.35) * mm, "end": v(30.58, 28.85) * mm});
            skLineSegment(sketch, "E8.0.2.23", {"start": v(20.22, 29.35) * mm, "end": v(30.58, 29.35) * mm});
            skLineSegment(sketch, "E8.3.2.23", {"start": v(20.22, 29.85) * mm, "end": v(30.58, 29.85) * mm});
            skLineSegment(sketch, "E8.6.2.23", {"start": v(20.22, 29.35) * mm, "end": v(20.22, 29.85) * mm});
            skLineSegment(sketch, "E8.9.2.23", {"start": v(30.58, 29.35) * mm, "end": v(30.58, 29.85) * mm});
            skLineSegment(sketch, "E8.0.2.24", {"start": v(20.22, 30.35) * mm, "end": v(30.58, 30.35) * mm});
            skLineSegment(sketch, "E8.3.2.24", {"start": v(20.22, 30.85) * mm, "end": v(30.58, 30.85) * mm});
            skLineSegment(sketch, "E8.6.2.24", {"start": v(20.22, 30.35) * mm, "end": v(20.22, 30.85) * mm});
            skLineSegment(sketch, "E8.9.2.24", {"start": v(30.58, 30.35) * mm, "end": v(30.58, 30.85) * mm});
            skLineSegment(sketch, "E8.0.2.25", {"start": v(20.22, 31.35) * mm, "end": v(30.58, 31.35) * mm});
            skLineSegment(sketch, "E8.3.2.25", {"start": v(20.22, 31.85) * mm, "end": v(30.58, 31.85) * mm});
            skLineSegment(sketch, "E8.6.2.25", {"start": v(20.22, 31.35) * mm, "end": v(20.22, 31.85) * mm});
            skLineSegment(sketch, "E8.9.2.25", {"start": v(30.58, 31.35) * mm, "end": v(30.58, 31.85) * mm});
            skLineSegment(sketch, "E8.0.2.26", {"start": v(20.22, 32.35) * mm, "end": v(30.58, 32.35) * mm});
            skLineSegment(sketch, "E8.3.2.26", {"start": v(20.22, 32.85) * mm, "end": v(30.58, 32.85) * mm});
            skLineSegment(sketch, "E8.6.2.26", {"start": v(20.22, 32.35) * mm, "end": v(20.22, 32.85) * mm});
            skLineSegment(sketch, "E8.9.2.26", {"start": v(30.58, 32.35) * mm, "end": v(30.58, 32.85) * mm});
            skLineSegment(sketch, "E8.0.2.27", {"start": v(20.22, 33.35) * mm, "end": v(30.58, 33.35) * mm});
            skLineSegment(sketch, "E8.3.2.27", {"start": v(20.22, 33.85) * mm, "end": v(30.58, 33.85) * mm});
            skLineSegment(sketch, "E8.6.2.27", {"start": v(20.22, 33.35) * mm, "end": v(20.22, 33.85) * mm});
            skLineSegment(sketch, "E8.9.2.27", {"start": v(30.58, 33.35) * mm, "end": v(30.58, 33.85) * mm});
            skLineSegment(sketch, "E8.0.2.28", {"start": v(20.22, 34.35) * mm, "end": v(30.58, 34.35) * mm});
            skLineSegment(sketch, "E8.3.2.28", {"start": v(20.22, 34.85) * mm, "end": v(30.58, 34.85) * mm});
            skLineSegment(sketch, "E8.6.2.28", {"start": v(20.22, 34.35) * mm, "end": v(20.22, 34.85) * mm});
            skLineSegment(sketch, "E8.9.2.28", {"start": v(30.58, 34.35) * mm, "end": v(30.58, 34.85) * mm});
            skLineSegment(sketch, "E8.0.2.29", {"start": v(20.22, 35.35) * mm, "end": v(30.58, 35.35) * mm});
            skLineSegment(sketch, "E8.3.2.29", {"start": v(20.22, 35.85) * mm, "end": v(30.58, 35.85) * mm});
            skLineSegment(sketch, "E8.6.2.29", {"start": v(20.22, 35.35) * mm, "end": v(20.22, 35.85) * mm});
            skLineSegment(sketch, "E8.9.2.29", {"start": v(30.58, 35.35) * mm, "end": v(30.58, 35.85) * mm});
            skLineSegment(sketch, "E8.0.2.30", {"start": v(20.22, 36.35) * mm, "end": v(30.58, 36.35) * mm});
            skLineSegment(sketch, "E8.3.2.30", {"start": v(20.22, 36.85) * mm, "end": v(30.58, 36.85) * mm});
            skLineSegment(sketch, "E8.6.2.30", {"start": v(20.22, 36.35) * mm, "end": v(20.22, 36.85) * mm});
            skLineSegment(sketch, "E8.9.2.30", {"start": v(30.58, 36.35) * mm, "end": v(30.58, 36.85) * mm});
            skLineSegment(sketch, "E8.0.2.31", {"start": v(20.22, 37.35) * mm, "end": v(30.58, 37.35) * mm});
            skLineSegment(sketch, "E8.3.2.31", {"start": v(20.22, 37.85) * mm, "end": v(30.58, 37.85) * mm});
            skLineSegment(sketch, "E8.6.2.31", {"start": v(20.22, 37.35) * mm, "end": v(20.22, 37.85) * mm});
            skLineSegment(sketch, "E8.9.2.31", {"start": v(30.58, 37.35) * mm, "end": v(30.58, 37.85) * mm});
            skLineSegment(sketch, "E8.0.2.32", {"start": v(20.22, 38.35) * mm, "end": v(30.58, 38.35) * mm});
            skLineSegment(sketch, "E8.3.2.32", {"start": v(20.22, 38.85) * mm, "end": v(30.58, 38.85) * mm});
            skLineSegment(sketch, "E8.6.2.32", {"start": v(20.22, 38.35) * mm, "end": v(20.22, 38.85) * mm});
            skLineSegment(sketch, "E8.9.2.32", {"start": v(30.58, 38.35) * mm, "end": v(30.58, 38.85) * mm});
            skLineSegment(sketch, "E8.0.2.33", {"start": v(20.22, 39.35) * mm, "end": v(30.58, 39.35) * mm});
            skLineSegment(sketch, "E8.3.2.33", {"start": v(20.22, 39.85) * mm, "end": v(30.58, 39.85) * mm});
            skLineSegment(sketch, "E8.6.2.33", {"start": v(20.22, 39.35) * mm, "end": v(20.22, 39.85) * mm});
            skLineSegment(sketch, "E8.9.2.33", {"start": v(30.58, 39.35) * mm, "end": v(30.58, 39.85) * mm});
            skLineSegment(sketch, "E8.0.2.34", {"start": v(20.22, 40.35) * mm, "end": v(30.58, 40.35) * mm});
            skLineSegment(sketch, "E8.3.2.34", {"start": v(20.22, 40.85) * mm, "end": v(30.58, 40.85) * mm});
            skLineSegment(sketch, "E8.6.2.34", {"start": v(20.22, 40.35) * mm, "end": v(20.22, 40.85) * mm});
            skLineSegment(sketch, "E8.9.2.34", {"start": v(30.58, 40.35) * mm, "end": v(30.58, 40.85) * mm});
            skLineSegment(sketch, "E8.0.2.35", {"start": v(20.22, 41.35) * mm, "end": v(30.58, 41.35) * mm});
            skLineSegment(sketch, "E8.3.2.35", {"start": v(20.22, 41.85) * mm, "end": v(30.58, 41.85) * mm});
            skLineSegment(sketch, "E8.6.2.35", {"start": v(20.22, 41.35) * mm, "end": v(20.22, 41.85) * mm});
            skLineSegment(sketch, "E8.9.2.35", {"start": v(30.58, 41.35) * mm, "end": v(30.58, 41.85) * mm});
            skLineSegment(sketch, "E8.0.2.36", {"start": v(20.22, 42.35) * mm, "end": v(30.58, 42.35) * mm});
            skLineSegment(sketch, "E8.3.2.36", {"start": v(20.22, 42.85) * mm, "end": v(30.58, 42.85) * mm});
            skLineSegment(sketch, "E8.6.2.36", {"start": v(20.22, 42.35) * mm, "end": v(20.22, 42.85) * mm});
            skLineSegment(sketch, "E8.9.2.36", {"start": v(30.58, 42.35) * mm, "end": v(30.58, 42.85) * mm});
            skLineSegment(sketch, "E8.0.2.37", {"start": v(20.22, 43.35) * mm, "end": v(30.58, 43.35) * mm});
            skLineSegment(sketch, "E8.3.2.37", {"start": v(20.22, 43.85) * mm, "end": v(30.58, 43.85) * mm});
            skLineSegment(sketch, "E8.6.2.37", {"start": v(20.22, 43.35) * mm, "end": v(20.22, 43.85) * mm});
            skLineSegment(sketch, "E8.9.2.37", {"start": v(30.58, 43.35) * mm, "end": v(30.58, 43.85) * mm});
            skLineSegment(sketch, "E8.0.2.38", {"start": v(20.22, 44.35) * mm, "end": v(30.58, 44.35) * mm});
            skLineSegment(sketch, "E8.3.2.38", {"start": v(20.22, 44.85) * mm, "end": v(30.58, 44.85) * mm});
            skLineSegment(sketch, "E8.6.2.38", {"start": v(20.22, 44.35) * mm, "end": v(20.22, 44.85) * mm});
            skLineSegment(sketch, "E8.9.2.38", {"start": v(30.58, 44.35) * mm, "end": v(30.58, 44.85) * mm});
            skLineSegment(sketch, "E8.0.2.39", {"start": v(20.22, 45.35) * mm, "end": v(30.58, 45.35) * mm});
            skLineSegment(sketch, "E8.3.2.39", {"start": v(20.22, 45.85) * mm, "end": v(30.58, 45.85) * mm});
            skLineSegment(sketch, "E8.6.2.39", {"start": v(20.22, 45.35) * mm, "end": v(20.22, 45.85) * mm});
            skLineSegment(sketch, "E8.9.2.39", {"start": v(30.58, 45.35) * mm, "end": v(30.58, 45.85) * mm});
            skLineSegment(sketch, "E8.0.2.40", {"start": v(20.22, 46.35) * mm, "end": v(30.58, 46.35) * mm});
            skLineSegment(sketch, "E8.3.2.40", {"start": v(20.22, 46.85) * mm, "end": v(30.58, 46.85) * mm});
            skLineSegment(sketch, "E8.6.2.40", {"start": v(20.22, 46.35) * mm, "end": v(20.22, 46.85) * mm});
            skLineSegment(sketch, "E8.9.2.40", {"start": v(30.58, 46.35) * mm, "end": v(30.58, 46.85) * mm});
            skLineSegment(sketch, "E8.0.2.41", {"start": v(20.22, 47.35) * mm, "end": v(30.58, 47.35) * mm});
            skLineSegment(sketch, "E8.3.2.41", {"start": v(20.22, 47.85) * mm, "end": v(30.58, 47.85) * mm});
            skLineSegment(sketch, "E8.6.2.41", {"start": v(20.22, 47.35) * mm, "end": v(20.22, 47.85) * mm});
            skLineSegment(sketch, "E8.9.2.41", {"start": v(30.58, 47.35) * mm, "end": v(30.58, 47.85) * mm});
            skLineSegment(sketch, "E8.0.2.42", {"start": v(20.22, 48.35) * mm, "end": v(30.58, 48.35) * mm});
            skLineSegment(sketch, "E8.3.2.42", {"start": v(20.22, 48.85) * mm, "end": v(30.58, 48.85) * mm});
            skLineSegment(sketch, "E8.6.2.42", {"start": v(20.22, 48.35) * mm, "end": v(20.22, 48.85) * mm});
            skLineSegment(sketch, "E8.9.2.42", {"start": v(30.58, 48.35) * mm, "end": v(30.58, 48.85) * mm});
            skLineSegment(sketch, "E8.0.2.43", {"start": v(20.22, 49.35) * mm, "end": v(30.58, 49.35) * mm});
            skLineSegment(sketch, "E8.3.2.43", {"start": v(20.22, 49.85) * mm, "end": v(30.58, 49.85) * mm});
            skLineSegment(sketch, "E8.6.2.43", {"start": v(20.22, 49.35) * mm, "end": v(20.22, 49.85) * mm});
            skLineSegment(sketch, "E8.9.2.43", {"start": v(30.58, 49.35) * mm, "end": v(30.58, 49.85) * mm});
            skLineSegment(sketch, "E8.0.2.44", {"start": v(20.22, 50.35) * mm, "end": v(30.58, 50.35) * mm});
            skLineSegment(sketch, "E8.3.2.44", {"start": v(20.22, 50.85) * mm, "end": v(30.58, 50.85) * mm});
            skLineSegment(sketch, "E8.6.2.44", {"start": v(20.22, 50.35) * mm, "end": v(20.22, 50.85) * mm});
            skLineSegment(sketch, "E8.9.2.44", {"start": v(30.58, 50.35) * mm, "end": v(30.58, 50.85) * mm});
            skLineSegment(sketch, "E8.0.2.45", {"start": v(20.22, 51.35) * mm, "end": v(30.58, 51.35) * mm});
            skLineSegment(sketch, "E8.3.2.45", {"start": v(20.22, 51.85) * mm, "end": v(30.58, 51.85) * mm});
            skLineSegment(sketch, "E8.6.2.45", {"start": v(20.22, 51.35) * mm, "end": v(20.22, 51.85) * mm});
            skLineSegment(sketch, "E8.9.2.45", {"start": v(30.58, 51.35) * mm, "end": v(30.58, 51.85) * mm});
            skLineSegment(sketch, "E8.0.2.46", {"start": v(20.22, 52.35) * mm, "end": v(30.58, 52.35) * mm});
            skLineSegment(sketch, "E8.3.2.46", {"start": v(20.22, 52.85) * mm, "end": v(30.58, 52.85) * mm});
            skLineSegment(sketch, "E8.6.2.46", {"start": v(20.22, 52.35) * mm, "end": v(20.22, 52.85) * mm});
            skLineSegment(sketch, "E8.9.2.46", {"start": v(30.58, 52.35) * mm, "end": v(30.58, 52.85) * mm});
            skLineSegment(sketch, "E8.0.2.47", {"start": v(20.22, 53.35) * mm, "end": v(30.58, 53.35) * mm});
            skLineSegment(sketch, "E8.3.2.47", {"start": v(20.22, 53.85) * mm, "end": v(30.58, 53.85) * mm});
            skLineSegment(sketch, "E8.6.2.47", {"start": v(20.22, 53.35) * mm, "end": v(20.22, 53.85) * mm});
            skLineSegment(sketch, "E8.9.2.47", {"start": v(30.58, 53.35) * mm, "end": v(30.58, 53.85) * mm});
            skLineSegment(sketch, "E8.0.2.48", {"start": v(20.22, 54.35) * mm, "end": v(30.58, 54.35) * mm});
            skLineSegment(sketch, "E8.3.2.48", {"start": v(20.22, 54.85) * mm, "end": v(30.58, 54.85) * mm});
            skLineSegment(sketch, "E8.6.2.48", {"start": v(20.22, 54.35) * mm, "end": v(20.22, 54.85) * mm});
            skLineSegment(sketch, "E8.9.2.48", {"start": v(30.58, 54.35) * mm, "end": v(30.58, 54.85) * mm});
            skLineSegment(sketch, "E8.0.2.49", {"start": v(20.22, 55.35) * mm, "end": v(30.58, 55.35) * mm});
            skLineSegment(sketch, "E8.3.2.49", {"start": v(20.22, 55.85) * mm, "end": v(30.58, 55.85) * mm});
            skLineSegment(sketch, "E8.6.2.49", {"start": v(20.22, 55.35) * mm, "end": v(20.22, 55.85) * mm});
            skLineSegment(sketch, "E8.9.2.49", {"start": v(30.58, 55.35) * mm, "end": v(30.58, 55.85) * mm});
            skLineSegment(sketch, "E8.0.2.50", {"start": v(20.22, 56.35) * mm, "end": v(30.58, 56.35) * mm});
            skLineSegment(sketch, "E8.3.2.50", {"start": v(20.22, 56.85) * mm, "end": v(30.58, 56.85) * mm});
            skLineSegment(sketch, "E8.6.2.50", {"start": v(20.22, 56.35) * mm, "end": v(20.22, 56.85) * mm});
            skLineSegment(sketch, "E8.9.2.50", {"start": v(30.58, 56.35) * mm, "end": v(30.58, 56.85) * mm});
            skLineSegment(sketch, "E8.0.2.51", {"start": v(20.22, 57.35) * mm, "end": v(30.58, 57.35) * mm});
            skLineSegment(sketch, "E8.3.2.51", {"start": v(20.22, 57.85) * mm, "end": v(30.58, 57.85) * mm});
            skLineSegment(sketch, "E8.6.2.51", {"start": v(20.22, 57.35) * mm, "end": v(20.22, 57.85) * mm});
            skLineSegment(sketch, "E8.9.2.51", {"start": v(30.58, 57.35) * mm, "end": v(30.58, 57.85) * mm});
            skLineSegment(sketch, "E8.0.2.52", {"start": v(20.22, 58.35) * mm, "end": v(30.58, 58.35) * mm});
            skLineSegment(sketch, "E8.3.2.52", {"start": v(20.22, 58.85) * mm, "end": v(30.58, 58.85) * mm});
            skLineSegment(sketch, "E8.6.2.52", {"start": v(20.22, 58.35) * mm, "end": v(20.22, 58.85) * mm});
            skLineSegment(sketch, "E8.9.2.52", {"start": v(30.58, 58.35) * mm, "end": v(30.58, 58.85) * mm});
            skLineSegment(sketch, "E8.0.2.53", {"start": v(20.22, 59.35) * mm, "end": v(30.58, 59.35) * mm});
            skLineSegment(sketch, "E8.3.2.53", {"start": v(20.22, 59.85) * mm, "end": v(30.58, 59.85) * mm});
            skLineSegment(sketch, "E8.6.2.53", {"start": v(20.22, 59.35) * mm, "end": v(20.22, 59.85) * mm});
            skLineSegment(sketch, "E8.9.2.53", {"start": v(30.58, 59.35) * mm, "end": v(30.58, 59.85) * mm});
            skLineSegment(sketch, "E8.0.2.54", {"start": v(20.22, 60.35) * mm, "end": v(30.58, 60.35) * mm});
            skLineSegment(sketch, "E8.3.2.54", {"start": v(20.22, 60.85) * mm, "end": v(30.58, 60.85) * mm});
            skLineSegment(sketch, "E8.6.2.54", {"start": v(20.22, 60.35) * mm, "end": v(20.22, 60.85) * mm});
            skLineSegment(sketch, "E8.9.2.54", {"start": v(30.58, 60.35) * mm, "end": v(30.58, 60.85) * mm});
            skLineSegment(sketch, "E8.0.2.55", {"start": v(20.22, 61.35) * mm, "end": v(30.58, 61.35) * mm});
            skLineSegment(sketch, "E8.3.2.55", {"start": v(20.22, 61.85) * mm, "end": v(30.58, 61.85) * mm});
            skLineSegment(sketch, "E8.6.2.55", {"start": v(20.22, 61.35) * mm, "end": v(20.22, 61.85) * mm});
            skLineSegment(sketch, "E8.9.2.55", {"start": v(30.58, 61.35) * mm, "end": v(30.58, 61.85) * mm});
            skLineSegment(sketch, "E8.0.2.56", {"start": v(20.22, 62.35) * mm, "end": v(30.58, 62.35) * mm});
            skLineSegment(sketch, "E8.3.2.56", {"start": v(20.22, 62.85) * mm, "end": v(30.58, 62.85) * mm});
            skLineSegment(sketch, "E8.6.2.56", {"start": v(20.22, 62.35) * mm, "end": v(20.22, 62.85) * mm});
            skLineSegment(sketch, "E8.9.2.56", {"start": v(30.58, 62.35) * mm, "end": v(30.58, 62.85) * mm});
            skLineSegment(sketch, "E8.0.2.57", {"start": v(20.22, 63.35) * mm, "end": v(30.58, 63.35) * mm});
            skLineSegment(sketch, "E8.3.2.57", {"start": v(20.22, 63.85) * mm, "end": v(30.58, 63.85) * mm});
            skLineSegment(sketch, "E8.6.2.57", {"start": v(20.22, 63.35) * mm, "end": v(20.22, 63.85) * mm});
            skLineSegment(sketch, "E8.9.2.57", {"start": v(30.58, 63.35) * mm, "end": v(30.58, 63.85) * mm});
            skLineSegment(sketch, "E8.0.2.58", {"start": v(20.22, 64.35) * mm, "end": v(30.58, 64.35) * mm});
            skLineSegment(sketch, "E8.3.2.58", {"start": v(20.22, 64.85) * mm, "end": v(30.58, 64.85) * mm});
            skLineSegment(sketch, "E8.6.2.58", {"start": v(20.22, 64.35) * mm, "end": v(20.22, 64.85) * mm});
            skLineSegment(sketch, "E8.9.2.58", {"start": v(30.58, 64.35) * mm, "end": v(30.58, 64.85) * mm});
            skLineSegment(sketch, "E8.0.2.59", {"start": v(20.22, 65.35) * mm, "end": v(30.58, 65.35) * mm});
            skLineSegment(sketch, "E8.3.2.59", {"start": v(20.22, 65.85) * mm, "end": v(30.58, 65.85) * mm});
            skLineSegment(sketch, "E8.6.2.59", {"start": v(20.22, 65.35) * mm, "end": v(20.22, 65.85) * mm});
            skLineSegment(sketch, "E8.9.2.59", {"start": v(30.58, 65.35) * mm, "end": v(30.58, 65.85) * mm});
            skLineSegment(sketch, "E8.0.2.60", {"start": v(20.22, 66.35) * mm, "end": v(30.58, 66.35) * mm});
            skLineSegment(sketch, "E8.3.2.60", {"start": v(20.22, 66.85) * mm, "end": v(30.58, 66.85) * mm});
            skLineSegment(sketch, "E8.6.2.60", {"start": v(20.22, 66.35) * mm, "end": v(20.22, 66.85) * mm});
            skLineSegment(sketch, "E8.9.2.60", {"start": v(30.58, 66.35) * mm, "end": v(30.58, 66.85) * mm});
            skLineSegment(sketch, "E8.0.2.61", {"start": v(20.22, 67.35) * mm, "end": v(30.58, 67.35) * mm});
            skLineSegment(sketch, "E8.3.2.61", {"start": v(20.22, 67.85) * mm, "end": v(30.58, 67.85) * mm});
            skLineSegment(sketch, "E8.6.2.61", {"start": v(20.22, 67.35) * mm, "end": v(20.22, 67.85) * mm});
            skLineSegment(sketch, "E8.9.2.61", {"start": v(30.58, 67.35) * mm, "end": v(30.58, 67.85) * mm});
            skLineSegment(sketch, "E8.0.2.62", {"start": v(20.22, 68.35) * mm, "end": v(30.58, 68.35) * mm});
            skLineSegment(sketch, "E8.3.2.62", {"start": v(20.22, 68.85) * mm, "end": v(30.58, 68.85) * mm});
            skLineSegment(sketch, "E8.6.2.62", {"start": v(20.22, 68.35) * mm, "end": v(20.22, 68.85) * mm});
            skLineSegment(sketch, "E8.9.2.62", {"start": v(30.58, 68.35) * mm, "end": v(30.58, 68.85) * mm});
            skLineSegment(sketch, "E8.0.2.63", {"start": v(20.22, 69.35) * mm, "end": v(30.58, 69.35) * mm});
            skLineSegment(sketch, "E8.3.2.63", {"start": v(20.22, 69.85) * mm, "end": v(30.58, 69.85) * mm});
            skLineSegment(sketch, "E8.6.2.63", {"start": v(20.22, 69.35) * mm, "end": v(20.22, 69.85) * mm});
            skLineSegment(sketch, "E8.9.2.63", {"start": v(30.58, 69.35) * mm, "end": v(30.58, 69.85) * mm});
            skLineSegment(sketch, "E8.0.2.64", {"start": v(20.22, 70.35) * mm, "end": v(30.58, 70.35) * mm});
            skLineSegment(sketch, "E8.3.2.64", {"start": v(20.22, 70.85) * mm, "end": v(30.58, 70.85) * mm});
            skLineSegment(sketch, "E8.6.2.64", {"start": v(20.22, 70.35) * mm, "end": v(20.22, 70.85) * mm});
            skLineSegment(sketch, "E8.9.2.64", {"start": v(30.58, 70.35) * mm, "end": v(30.58, 70.85) * mm});
            skLineSegment(sketch, "E8.0.2.65", {"start": v(20.22, 71.35) * mm, "end": v(30.58, 71.35) * mm});
            skLineSegment(sketch, "E8.3.2.65", {"start": v(20.22, 71.85) * mm, "end": v(30.58, 71.85) * mm});
            skLineSegment(sketch, "E8.6.2.65", {"start": v(20.22, 71.35) * mm, "end": v(20.22, 71.85) * mm});
            skLineSegment(sketch, "E8.9.2.65", {"start": v(30.58, 71.35) * mm, "end": v(30.58, 71.85) * mm});
            skLineSegment(sketch, "E8.0.2.66", {"start": v(20.22, 72.35) * mm, "end": v(30.58, 72.35) * mm});
            skLineSegment(sketch, "E8.3.2.66", {"start": v(20.22, 72.85) * mm, "end": v(30.58, 72.85) * mm});
            skLineSegment(sketch, "E8.6.2.66", {"start": v(20.22, 72.35) * mm, "end": v(20.22, 72.85) * mm});
            skLineSegment(sketch, "E8.9.2.66", {"start": v(30.58, 72.35) * mm, "end": v(30.58, 72.85) * mm});
            skLineSegment(sketch, "E8.0.2.67", {"start": v(20.22, 73.35) * mm, "end": v(30.58, 73.35) * mm});
            skLineSegment(sketch, "E8.3.2.67", {"start": v(20.22, 73.85) * mm, "end": v(30.58, 73.85) * mm});
            skLineSegment(sketch, "E8.6.2.67", {"start": v(20.22, 73.35) * mm, "end": v(20.22, 73.85) * mm});
            skLineSegment(sketch, "E8.9.2.67", {"start": v(30.58, 73.35) * mm, "end": v(30.58, 73.85) * mm});
            skLineSegment(sketch, "E8.0.2.68", {"start": v(20.22, 74.35) * mm, "end": v(30.58, 74.35) * mm});
            skLineSegment(sketch, "E8.3.2.68", {"start": v(20.22, 74.85) * mm, "end": v(30.58, 74.85) * mm});
            skLineSegment(sketch, "E8.6.2.68", {"start": v(20.22, 74.35) * mm, "end": v(20.22, 74.85) * mm});
            skLineSegment(sketch, "E8.9.2.68", {"start": v(30.58, 74.35) * mm, "end": v(30.58, 74.85) * mm});
            skSolve(sketch);
        }
        {
            var Q0;
            Q0 = qSketchRegion(id + "F4", true);
            var Q1;
            Q1=makeQuery(id+"F1.opExtrude","SWEPT_FACE",FACE,{"disambiguationData":[OSD([sQuery(id+"F0.wireOp",EDGE,"E0.bottom")])]});
            extrude(context, id + "F5", {"entities" : qUnion([Q0]), "operationType" : NewBodyOperationType.REMOVE, "endBound" : BoundingType.UP_TO_SURFACE, "oppositeDirection" : true, "depth" : 25.4 * mm, "endBoundEntityFace" : qUnion([Q1]), "offsetDistance" : 25.4 * mm});
        }
        {
            var Q0;
            Q0=makeQuery(id+"F1.opExtrude","SWEPT_FACE",FACE,{"disambiguationData":[OSD([sQuery(id+"F0.wireOp",EDGE,"E0.top")])]});
            var sketch = newSketch(context, id + "F6", { "sketchPlane" : qUnion([Q0])});
            skText(sketch, "E9", { "text": "1", "fontName": "OpenSans-Regular.ttf"});
            skText(sketch, "E10", { "text": "2", "fontName": "OpenSans-Regular.ttf"});
            skText(sketch, "E11", { "text": "3", "fontName": "OpenSans-Regular.ttf"});
            const initialGuessF6  = {"E9": [-0.02685, 0.00156, 1, 0, 0.00381], "E10": [-0.00154, 0.00156, 1, 0, 0.00381], "E11": [0.02409, 0.00156, 1, 0, 0.00381]};
            skSetInitialGuess(sketch, initialGuessF6);
            skSolve(sketch);
        }
        {
            var Q0;
            Q0 = qSketchRegion(id + "F6", true);
            extrude(context, id + "F7", {"entities" : qUnion([Q0]), "operationType" : NewBodyOperationType.REMOVE, "oppositeDirection" : true, "depth" : 0.5 * mm, "offsetDistance" : 25.4 * mm});
        }
        {
            var Q0;
            Q0=makeQuery(id+"F1.opExtrude","CAP_FACE",FACE,{"disambiguationData":[OSD([sQuery(id+"F0.wireOp",EDGE,"E0.bottom"),sQuery(id+"F0.wireOp",EDGE,"E0.top"),sQuery(id+"F0.wireOp",EDGE,"E0.left"),sQuery(id+"F0.wireOp",EDGE,"E0.right")])],"isStart":false});
            var sketch = newSketch(context, id + "F8", { "sketchPlane" : qUnion([Q0])});
            skLineSegment(sketch, "E12.bottom", {"start": v(30.58, 1.5) * mm, "end": v(20.22, 1.5) * mm});
            skLineSegment(sketch, "E12.top", {"start": v(30.58, 5) * mm, "end": v(20.22, 5) * mm});
            skLineSegment(sketch, "E12.left", {"start": v(30.58, 1.5) * mm, "end": v(30.58, 5) * mm});
            skLineSegment(sketch, "E12.right", {"start": v(20.22, 1.5) * mm, "end": v(20.22, 5) * mm});
            skLineSegment(sketch, "E13.1.0.0", {"start": v(5.18, 1.5) * mm, "end": v(-5.18, 1.5) * mm});
            skLineSegment(sketch, "E13.1.0.1", {"start": v(-5.18, 1.5) * mm, "end": v(-5.18, 5) * mm});
            skLineSegment(sketch, "E13.1.0.2", {"start": v(5.18, 1.5) * mm, "end": v(5.18, 5) * mm});
            skLineSegment(sketch, "E13.1.0.3", {"start": v(5.18, 5) * mm, "end": v(-5.18, 5) * mm});
            skLineSegment(sketch, "E13.2.0.0", {"start": v(-20.22, 1.5) * mm, "end": v(-30.58, 1.5) * mm});
            skLineSegment(sketch, "E13.2.0.1", {"start": v(-30.58, 1.5) * mm, "end": v(-30.58, 5) * mm});
            skLineSegment(sketch, "E13.2.0.2", {"start": v(-20.22, 1.5) * mm, "end": v(-20.22, 5) * mm});
            skLineSegment(sketch, "E13.2.0.3", {"start": v(-20.22, 5) * mm, "end": v(-30.58, 5) * mm});
            skLineSegment(sketch, "E13.direction1", {"start": v(20.22, 1.5) * mm, "end": v(-5.18, 1.5) * mm, "construction": true});
            skSolve(sketch);
        }
        {
            var Q0;
            Q0 = qSketchRegion(id + "F8", true);
            var Q1;
            Q1=makeQuery(id+"F5.boolean.opBoolean","MERGE",FACE,{"derivedFrom":[makeQuery(id+"F3.boolean.opBoolean","COPY",FACE,{"derivedFrom":makeQuery(id+"F3.opExtrude","CAP_FACE",FACE,{"disambiguationData":[OSD([sQuery(id+"F2.wireOp",EDGE,"E4")])],"isStart":false})})],"fromTools":[makeQuery(id+"F5.opExtrude","SWEPT_FACE",FACE,{"disambiguationData":[OSD([sQuery(id+"F4.wireOp",EDGE,"E5.bottom")])]})]});
            extrude(context, id + "F9", {"entities" : qUnion([Q0]), "operationType" : NewBodyOperationType.REMOVE, "endBound" : BoundingType.UP_TO_SURFACE, "oppositeDirection" : true, "depth" : 25.4 * mm, "endBoundEntityFace" : qUnion([Q1]), "offsetDistance" : 25.4 * mm});
        }
        {
            var Q0;
            Q0=makeQuery(id+"F1.opExtrude","SWEPT_FACE",FACE,{"disambiguationData":[OSD([sQuery(id+"F0.wireOp",EDGE,"E0.left")])]});
            var sketch = newSketch(context, id + "F10", { "sketchPlane" : qUnion([Q0])});
            skLineSegment(sketch, "E14.bottom", {"start": v(-5.5, 0) * mm, "end": v(5.5, 0) * mm});
            skLineSegment(sketch, "E14.top", {"start": v(-5.5, 6.35) * mm, "end": v(5.5, 6.35) * mm});
            skLineSegment(sketch, "E14.left", {"start": v(-5.5, 0) * mm, "end": v(-5.5, 6.35) * mm});
            skLineSegment(sketch, "E14.right", {"start": v(5.5, 0) * mm, "end": v(5.5, 6.35) * mm});
            skSolve(sketch);
        }
        {
            var Q0;
            Q0 = qSketchRegion(id + "F10", true);
            extrude(context, id + "F11", {"entities" : qUnion([Q0]), "operationType" : NewBodyOperationType.ADD, "depth" : 12.7 * mm, "offsetDistance" : 25.4 * mm});
        }
        {
            var Q0;
            Q0=makeQuery(id+"F1.opExtrude","SWEPT_FACE",FACE,{"disambiguationData":[OSD([sQuery(id+"F0.wireOp",EDGE,"E0.right")])]});
            var sketch = newSketch(context, id + "F12", { "sketchPlane" : qUnion([Q0])});
            skLineSegment(sketch, "E15.bottom", {"start": v(-5.5, 0) * mm, "end": v(5.5, 0) * mm});
            skLineSegment(sketch, "E15.top", {"start": v(-5.5, 6.35) * mm, "end": v(5.5, 6.35) * mm});
            skLineSegment(sketch, "E15.left", {"start": v(-5.5, 0) * mm, "end": v(-5.5, 6.35) * mm});
            skLineSegment(sketch, "E15.right", {"start": v(5.5, 0) * mm, "end": v(5.5, 6.35) * mm});
            skSolve(sketch);
        }
        {
            var Q0;
            Q0 = qSketchRegion(id + "F12", true);
            extrude(context, id + "F13", {"entities" : qUnion([Q0]), "operationType" : NewBodyOperationType.ADD, "depth" : 12.7 * mm, "offsetDistance" : 25.4 * mm});
        }
        {
            var Q0;
            Q0=makeQuery(id+"F13.opExtrude","SWEPT_FACE",FACE,{"disambiguationData":[OSD([sQuery(id+"F12.wireOp",EDGE,"E15.top")])]});
            var sketch = newSketch(context, id + "F14", { "sketchPlane" : qUnion([Q0])});
            skCircle(sketch, "E16", {"center": v(-44.45, 0) * mm, "radius": 2.05 * mm});
            skPoint(sketch, "E17", {"position": v(-38.1, 0) * mm});
            skLineSegment(sketch, "E18", {"start": v(-44.45, 5.5) * mm, "end": v(-44.45, -5.5) * mm});
            skCircle(sketch, "E19.MirrorC", {"center": v(44.45, 0) * mm, "radius": 2.05 * mm});
            skSolve(sketch);
        }
        {
            var Q0;
            Q0 = qSketchRegion(id + "F14", true);
            extrude(context, id + "F15", {"entities" : qUnion([Q0]), "operationType" : NewBodyOperationType.REMOVE, "endBound" : BoundingType.UP_TO_NEXT, "oppositeDirection" : true, "depth" : 25.4 * mm, "offsetDistance" : 25.4 * mm});
        }
    });
